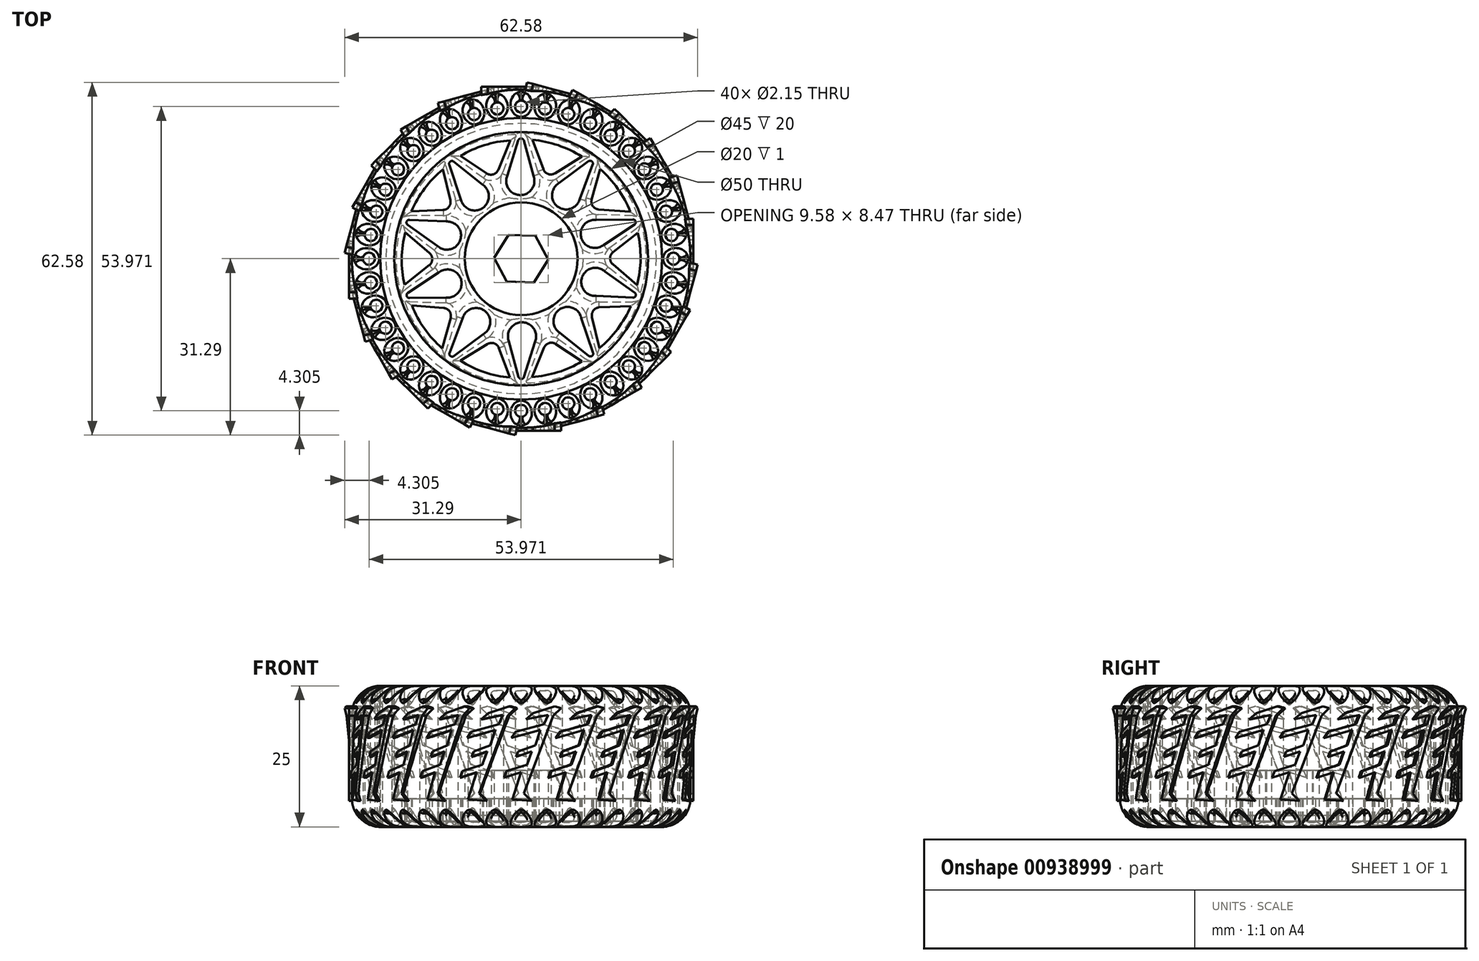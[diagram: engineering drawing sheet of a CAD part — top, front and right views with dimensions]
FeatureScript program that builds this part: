
annotation { "Feature Type Name" : "Feature", "Feature Type Description" : "" }
export const myFeature = defineFeature(function(context is Context, id is Id, definition is map)
    precondition{}
    {
        {
            var Q0;
            Q0=qCreatedBy(makeId("Top.planeOp"),FACE);
            var sketch = newSketch(context, id + "F0", { "sketchPlane" : qUnion([Q0])});
            skCircle(sketch, "E0", {"center": v(0, 0) * mm, "radius": 25 * mm});
            skCircle(sketch, "E1", {"center": v(0, 0) * mm, "radius": 22.5 * mm});
            skCircle(sketch, "E2", {"center": v(0, 0) * mm, "radius": 10 * mm});
            skLineSegment(sketch, "E3", {"start": v(0, 10) * mm, "end": v(0, 22.5) * mm, "construction": true});
            skPoint(sketch, "E4", {"position": v(0, 16.25) * mm});
            skCircle(sketch, "E5", {"center": v(-0.16, 13.78) * mm, "radius": 2.5 * mm});
            skPoint(sketch, "E6", {"position": v(0, 22.61) * mm});
            skLineSegment(sketch, "E7", {"start": v(-2.63, 14.21) * mm, "end": v(2.3, 14.21) * mm, "construction": true});
            skLineSegment(sketch, "E8", {"start": v(-0.5, 20.99) * mm, "end": v(-2.63, 14.21) * mm});
            skLineSegment(sketch, "E9", {"start": v(0.45, 20.97) * mm, "end": v(2.3, 14.21) * mm});
            skArc(sketch, "E10.filletArc", {"start": v(0.45, 20.97) * mm, "mid": v(-0.02, 21.34) * mm, "end": v(-0.5, 20.99) * mm});
            skCircle(sketch, "E11.1.0", {"center": v(-8.23, 11.06) * mm, "radius": 2.5 * mm});
            skLineSegment(sketch, "E11.1.1", {"start": v(-11.96, 17.23) * mm, "end": v(-6.49, 12.85) * mm});
            skLineSegment(sketch, "E11.1.2", {"start": v(-12.75, 16.68) * mm, "end": v(-10.48, 9.95) * mm});
            skArc(sketch, "E11.1.3", {"start": v(-11.96, 17.23) * mm, "mid": v(-12.56, 17.25) * mm, "end": v(-12.75, 16.68) * mm});
            skCircle(sketch, "E11.2.0", {"center": v(-13.15, 4.11) * mm, "radius": 2.5 * mm});
            skLineSegment(sketch, "E11.2.1", {"start": v(-19.8, 6.9) * mm, "end": v(-12.8, 6.59) * mm});
            skLineSegment(sketch, "E11.2.2", {"start": v(-20.12, 6) * mm, "end": v(-14.33, 1.9) * mm});
            skArc(sketch, "E11.2.3", {"start": v(-19.8, 6.9) * mm, "mid": v(-20.3, 6.57) * mm, "end": v(-20.12, 6) * mm});
            skCircle(sketch, "E11.3.0", {"center": v(-13.06, -4.4) * mm, "radius": 2.5 * mm});
            skLineSegment(sketch, "E11.3.1", {"start": v(-20.08, -6.05) * mm, "end": v(-14.23, -2.2) * mm});
            skLineSegment(sketch, "E11.3.2", {"start": v(-19.8, -6.97) * mm, "end": v(-12.7, -6.89) * mm});
            skArc(sketch, "E11.3.3", {"start": v(-20.08, -6.05) * mm, "mid": v(-20.29, -6.61) * mm, "end": v(-19.8, -6.97) * mm});
            skCircle(sketch, "E11.4.0", {"center": v(-7.97, -11.24) * mm, "radius": 2.5 * mm});
            skLineSegment(sketch, "E11.4.1", {"start": v(-12.7, -16.7) * mm, "end": v(-10.22, -10.14) * mm});
            skLineSegment(sketch, "E11.4.2", {"start": v(-11.92, -17.28) * mm, "end": v(-6.23, -13.04) * mm});
            skArc(sketch, "E11.4.3", {"start": v(-12.7, -16.7) * mm, "mid": v(-12.52, -17.28) * mm, "end": v(-11.92, -17.28) * mm});
            skCircle(sketch, "E11.5.0", {"center": v(0.16, -13.78) * mm, "radius": 2.5 * mm});
            skLineSegment(sketch, "E11.5.1", {"start": v(-0.45, -20.97) * mm, "end": v(-2.3, -14.21) * mm});
            skLineSegment(sketch, "E11.5.2", {"start": v(0.5, -20.99) * mm, "end": v(2.63, -14.21) * mm});
            skArc(sketch, "E11.5.3", {"start": v(-0.45, -20.97) * mm, "mid": v(0.02, -21.34) * mm, "end": v(0.5, -20.99) * mm});
            skCircle(sketch, "E11.6.0", {"center": v(8.23, -11.06) * mm, "radius": 2.5 * mm});
            skLineSegment(sketch, "E11.6.1", {"start": v(11.96, -17.23) * mm, "end": v(6.49, -12.85) * mm});
            skLineSegment(sketch, "E11.6.2", {"start": v(12.75, -16.68) * mm, "end": v(10.48, -9.95) * mm});
            skArc(sketch, "E11.6.3", {"start": v(11.96, -17.23) * mm, "mid": v(12.56, -17.25) * mm, "end": v(12.75, -16.68) * mm});
            skCircle(sketch, "E11.7.0", {"center": v(13.15, -4.11) * mm, "radius": 2.5 * mm});
            skLineSegment(sketch, "E11.7.1", {"start": v(19.8, -6.9) * mm, "end": v(12.8, -6.59) * mm});
            skLineSegment(sketch, "E11.7.2", {"start": v(20.12, -6) * mm, "end": v(14.33, -1.9) * mm});
            skArc(sketch, "E11.7.3", {"start": v(19.8, -6.9) * mm, "mid": v(20.3, -6.57) * mm, "end": v(20.12, -6) * mm});
            skCircle(sketch, "E11.8.0", {"center": v(13.06, 4.4) * mm, "radius": 2.5 * mm});
            skLineSegment(sketch, "E11.8.1", {"start": v(20.08, 6.05) * mm, "end": v(14.23, 2.2) * mm});
            skLineSegment(sketch, "E11.8.2", {"start": v(19.8, 6.97) * mm, "end": v(12.7, 6.89) * mm});
            skArc(sketch, "E11.8.3", {"start": v(20.08, 6.05) * mm, "mid": v(20.29, 6.61) * mm, "end": v(19.8, 6.97) * mm});
            skCircle(sketch, "E11.9.0", {"center": v(7.97, 11.24) * mm, "radius": 2.5 * mm});
            skLineSegment(sketch, "E11.9.1", {"start": v(12.7, 16.7) * mm, "end": v(10.22, 10.14) * mm});
            skLineSegment(sketch, "E11.9.2", {"start": v(11.92, 17.28) * mm, "end": v(6.23, 13.04) * mm});
            skArc(sketch, "E11.9.3", {"start": v(12.7, 16.7) * mm, "mid": v(12.52, 17.28) * mm, "end": v(11.92, 17.28) * mm});
            skLineSegment(sketch, "E12", {"start": v(-10.78, 18.23) * mm, "end": v(-6.12, 15.12) * mm});
            skPoint(sketch, "E12.endSnap0", {"position": v(-9.22, 15.04) * mm});
            skLineSegment(sketch, "E13", {"start": v(-1.93, 20.97) * mm, "end": v(-4.06, 15.78) * mm});
            skArc(sketch, "E14", {"start": v(-6.12, 15.12) * mm, "mid": v(-4.94, 14.97) * mm, "end": v(-4.06, 15.78) * mm});
            skArc(sketch, "E15", {"start": v(-1.93, 20.97) * mm, "mid": v(-6.52, 20.14) * mm, "end": v(-10.78, 18.23) * mm});
            skLineSegment(sketch, "E16.1.0", {"start": v(-19.44, 8.41) * mm, "end": v(-13.84, 8.64) * mm});
            skArc(sketch, "E16.1.1", {"start": v(-13.84, 8.64) * mm, "mid": v(-12.8, 9.21) * mm, "end": v(-12.56, 10.38) * mm});
            skLineSegment(sketch, "E16.1.2", {"start": v(-13.9, 15.83) * mm, "end": v(-12.56, 10.38) * mm});
            skArc(sketch, "E16.1.3", {"start": v(-13.9, 15.83) * mm, "mid": v(-17.11, 12.46) * mm, "end": v(-19.44, 8.41) * mm});
            skLineSegment(sketch, "E16.2.0", {"start": v(-20.67, -4.62) * mm, "end": v(-16.27, -1.15) * mm});
            skArc(sketch, "E16.2.1", {"start": v(-16.27, -1.15) * mm, "mid": v(-15.76, -0.07) * mm, "end": v(-16.26, 1.01) * mm});
            skLineSegment(sketch, "E16.2.2", {"start": v(-20.54, 4.65) * mm, "end": v(-16.26, 1.01) * mm});
            skArc(sketch, "E16.2.3", {"start": v(-20.54, 4.65) * mm, "mid": v(-21.17, 0.02) * mm, "end": v(-20.67, -4.62) * mm});
            skLineSegment(sketch, "E16.3.0", {"start": v(-14, -15.89) * mm, "end": v(-12.5, -10.5) * mm});
            skArc(sketch, "E16.3.1", {"start": v(-12.5, -10.5) * mm, "mid": v(-12.71, -9.32) * mm, "end": v(-13.75, -8.74) * mm});
            skLineSegment(sketch, "E16.3.2", {"start": v(-19.35, -8.32) * mm, "end": v(-13.75, -8.74) * mm});
            skArc(sketch, "E16.3.3", {"start": v(-19.35, -8.32) * mm, "mid": v(-17.14, -12.42) * mm, "end": v(-14, -15.89) * mm});
            skLineSegment(sketch, "E16.4.0", {"start": v(-2, -21.09) * mm, "end": v(-3.94, -15.83) * mm});
            skArc(sketch, "E16.4.1", {"start": v(-3.94, -15.83) * mm, "mid": v(-4.8, -15.01) * mm, "end": v(-5.99, -15.15) * mm});
            skLineSegment(sketch, "E16.4.2", {"start": v(-10.77, -18.1) * mm, "end": v(-5.99, -15.15) * mm});
            skArc(sketch, "E16.4.3", {"start": v(-10.77, -18.1) * mm, "mid": v(-6.56, -20.12) * mm, "end": v(-2, -21.09) * mm});
            skLineSegment(sketch, "E16.5.0", {"start": v(10.78, -18.23) * mm, "end": v(6.12, -15.12) * mm});
            skArc(sketch, "E16.5.1", {"start": v(6.12, -15.12) * mm, "mid": v(4.94, -14.97) * mm, "end": v(4.06, -15.78) * mm});
            skLineSegment(sketch, "E16.5.2", {"start": v(1.93, -20.97) * mm, "end": v(4.06, -15.78) * mm});
            skArc(sketch, "E16.5.3", {"start": v(1.93, -20.97) * mm, "mid": v(6.52, -20.14) * mm, "end": v(10.78, -18.23) * mm});
            skLineSegment(sketch, "E16.6.0", {"start": v(19.44, -8.41) * mm, "end": v(13.84, -8.64) * mm});
            skArc(sketch, "E16.6.1", {"start": v(13.84, -8.64) * mm, "mid": v(12.8, -9.21) * mm, "end": v(12.56, -10.38) * mm});
            skLineSegment(sketch, "E16.6.2", {"start": v(13.9, -15.83) * mm, "end": v(12.56, -10.38) * mm});
            skArc(sketch, "E16.6.3", {"start": v(13.9, -15.83) * mm, "mid": v(17.11, -12.46) * mm, "end": v(19.44, -8.41) * mm});
            skLineSegment(sketch, "E16.7.0", {"start": v(20.67, 4.62) * mm, "end": v(16.27, 1.15) * mm});
            skArc(sketch, "E16.7.1", {"start": v(16.27, 1.15) * mm, "mid": v(15.76, 0.07) * mm, "end": v(16.26, -1.01) * mm});
            skLineSegment(sketch, "E16.7.2", {"start": v(20.54, -4.65) * mm, "end": v(16.26, -1.01) * mm});
            skArc(sketch, "E16.7.3", {"start": v(20.54, -4.65) * mm, "mid": v(21.17, -0.02) * mm, "end": v(20.67, 4.62) * mm});
            skLineSegment(sketch, "E16.8.0", {"start": v(14, 15.89) * mm, "end": v(12.5, 10.5) * mm});
            skArc(sketch, "E16.8.1", {"start": v(12.5, 10.5) * mm, "mid": v(12.71, 9.32) * mm, "end": v(13.75, 8.74) * mm});
            skLineSegment(sketch, "E16.8.2", {"start": v(19.35, 8.32) * mm, "end": v(13.75, 8.74) * mm});
            skArc(sketch, "E16.8.3", {"start": v(19.35, 8.32) * mm, "mid": v(17.14, 12.42) * mm, "end": v(14, 15.89) * mm});
            skLineSegment(sketch, "E16.9.0", {"start": v(2, 21.09) * mm, "end": v(3.94, 15.83) * mm});
            skArc(sketch, "E16.9.1", {"start": v(3.94, 15.83) * mm, "mid": v(4.8, 15.01) * mm, "end": v(5.99, 15.15) * mm});
            skLineSegment(sketch, "E16.9.2", {"start": v(10.77, 18.1) * mm, "end": v(5.99, 15.15) * mm});
            skArc(sketch, "E16.9.3", {"start": v(10.77, 18.1) * mm, "mid": v(6.56, 20.12) * mm, "end": v(2, 21.09) * mm});
            skCircle(sketch, "E17", {"center": v(0, 0) * mm, "radius": 30 * mm});
            skSolve(sketch);
        }
        {
            var Q0;
            Q0=makeQuery(id+"F0.imprint","IMPRINT",FACE,{"disambiguationData":[TD([[makeQuery(id+"F0.imprint","IMPRINT",EDGE,{"derivedFrom":sQuery(id+"F0.wireOp",EDGE,"E0")}),1.0]])]});
            extrude(context, id + "F1", {"entities" : qUnion([Q0]), "depth" : 25 * mm, "offsetDistance" : 25 * mm});
        }
        {
            var Q0;
            Q0=makeQuery(id+"F0.imprint","IMPRINT",FACE,{"disambiguationData":[TD([[makeQuery(id+"F0.imprint","IMPRINT",EDGE,{"derivedFrom":sQuery(id+"F0.wireOp",EDGE,"E1")}),1.0]])]});
            extrude(context, id + "F2", {"entities" : qUnion([Q0]), "operationType" : NewBodyOperationType.ADD, "depth" : 5 * mm, "offsetDistance" : 25 * mm});
        }
        {
            var Q0;
            {var subQ0=sQuery(id+"F0.wireOp",EDGE,"E2");var subQ1=makeQuery(id+"F0.imprint","INTERSECT",VERTEX,{"derivedFrom":[subQ0,sQuery(id+"F0.wireOp",EDGE,"FMw9U3Ag-M4uU-eOUw-AIyu-Y3kzjyrUIhWa.right")]});Q0=makeQuery(id+"F0.imprint","IMPRINT",FACE,{"disambiguationData":[TD([[makeQuery(id+"F0.imprint","IMPRINT",EDGE,{"disambiguationData":[TD([[subQ1,1.0]])],"derivedFrom":subQ0}),1.0]])]});}
            extrude(context, id + "F3", {"entities" : qUnion([Q0]), "operationType" : NewBodyOperationType.ADD, "depth" : 10 * mm, "offsetDistance" : 25 * mm});
        }
        {
            var Q0;
            Q0=makeQuery(id+"F0.imprint","IMPRINT",FACE,{"disambiguationData":[TD([[makeQuery(id+"F0.imprint","IMPRINT",EDGE,{"derivedFrom":sQuery(id+"F0.wireOp",EDGE,"E2")}),1.0]])]});
            extrude(context, id + "F4", {"entities" : qUnion([Q0]), "operationType" : NewBodyOperationType.REMOVE, "depth" : 2 * mm, "offsetDistance" : 25 * mm});
        }
        {
            var Q0;
            Q0=makeQuery(id+"F0.imprint","IMPRINT",FACE,{"disambiguationData":[TD([[makeQuery(id+"F0.imprint","IMPRINT",EDGE,{"derivedFrom":sQuery(id+"F0.wireOp",EDGE,"E2")}),1.0]])]});
            var sketch = newSketch(context, id + "F5", { "sketchPlane" : qUnion([Q0])});
            skPoint(sketch, "E18.0.midPoint", {"position": v(-3.35, 1.99) * mm});
            skCircle(sketch, "E19.cCircle", {"center": v(0, 0) * mm, "radius": 4.15 * mm, "construction": true});
            skLineSegment(sketch, "E19.0", {"start": v(-4.79, 0.17) * mm, "end": v(-2.25, 4.23) * mm});
            skLineSegment(sketch, "E19.1", {"start": v(-2.25, 4.23) * mm, "end": v(2.54, 4.06) * mm});
            skLineSegment(sketch, "E19.2", {"start": v(2.54, 4.06) * mm, "end": v(4.79, -0.17) * mm});
            skLineSegment(sketch, "E19.3", {"start": v(4.79, -0.17) * mm, "end": v(2.25, -4.23) * mm});
            skLineSegment(sketch, "E19.4", {"start": v(2.25, -4.23) * mm, "end": v(-2.54, -4.06) * mm});
            skLineSegment(sketch, "E19.5", {"start": v(-2.54, -4.06) * mm, "end": v(-4.79, 0.17) * mm});
            skPoint(sketch, "E19.0.midPoint", {"position": v(-3.52, 2.2) * mm});
            skPoint(sketch, "E20.orphan", {"position": v(-2.3, -3.87) * mm});
            skPoint(sketch, "E21.orphan", {"position": v(2.2, -3.92) * mm});
            skPoint(sketch, "E22.orphan", {"position": v(-4.5, 0.05) * mm});
            skPoint(sketch, "E18.1.start.orphan", {"position": v(-2.2, 3.92) * mm});
            skSolve(sketch);
        }
        {
            var Q0;
            Q0=makeQuery(id+"F5.imprint","IMPRINT",FACE,{"disambiguationData":[TD([[makeQuery(id+"F5.imprint","IMPRINT",EDGE,{"derivedFrom":sQuery(id+"F5.wireOp",EDGE,"E19.0")}),-1.0]])]});
            extrude(context, id + "F6", {"entities" : qUnion([Q0]), "operationType" : NewBodyOperationType.REMOVE, "depth" : 25 * mm, "offsetDistance" : 25 * mm});
        }
        {
            var Q0;
            {var subQ0=sQuery(id+"F0.wireOp",EDGE,"E2");var subQ1=sQuery(id+"F0.wireOp",EDGE,"E1");Q0=makeQuery(id+"F3.boolean.opBoolean","MERGE",FACE,{"derivedFrom":[makeQuery(id+"F2.boolean.opBoolean","MERGE",FACE,{"derivedFrom":[makeQuery(id+"F1.opExtrude","CAP_FACE",FACE,{"disambiguationData":[OSD([sQuery(id+"F0.wireOp",EDGE,"E0"),subQ1])],"isStart":true}),makeQuery(id+"F2.opExtrude","CAP_FACE",FACE,{"disambiguationData":[OSD([subQ1,subQ0,sQuery(id+"F0.wireOp",EDGE,"E5"),sQuery(id+"F0.wireOp",EDGE,"E8"),sQuery(id+"F0.wireOp",EDGE,"E9"),sQuery(id+"F0.wireOp",EDGE,"E10.filletArc"),sQuery(id+"F0.wireOp",EDGE,"E11.1.0"),sQuery(id+"F0.wireOp",EDGE,"E11.1.1"),sQuery(id+"F0.wireOp",EDGE,"E11.1.2"),sQuery(id+"F0.wireOp",EDGE,"E11.1.3"),sQuery(id+"F0.wireOp",EDGE,"E11.2.0"),sQuery(id+"F0.wireOp",EDGE,"E11.2.1"),sQuery(id+"F0.wireOp",EDGE,"E11.2.2"),sQuery(id+"F0.wireOp",EDGE,"E11.2.3"),sQuery(id+"F0.wireOp",EDGE,"E11.3.0"),sQuery(id+"F0.wireOp",EDGE,"E11.3.1"),sQuery(id+"F0.wireOp",EDGE,"E11.3.2"),sQuery(id+"F0.wireOp",EDGE,"E11.3.3"),sQuery(id+"F0.wireOp",EDGE,"E11.4.0"),sQuery(id+"F0.wireOp",EDGE,"E11.4.1"),sQuery(id+"F0.wireOp",EDGE,"E11.4.2"),sQuery(id+"F0.wireOp",EDGE,"E11.4.3"),sQuery(id+"F0.wireOp",EDGE,"E11.5.0"),sQuery(id+"F0.wireOp",EDGE,"E11.5.1"),sQuery(id+"F0.wireOp",EDGE,"E11.5.2"),sQuery(id+"F0.wireOp",EDGE,"E11.5.3"),sQuery(id+"F0.wireOp",EDGE,"E11.6.0"),sQuery(id+"F0.wireOp",EDGE,"E11.6.1"),sQuery(id+"F0.wireOp",EDGE,"E11.6.2"),sQuery(id+"F0.wireOp",EDGE,"E11.6.3"),sQuery(id+"F0.wireOp",EDGE,"E11.7.0"),sQuery(id+"F0.wireOp",EDGE,"E11.7.1"),sQuery(id+"F0.wireOp",EDGE,"E11.7.2"),sQuery(id+"F0.wireOp",EDGE,"E11.7.3"),sQuery(id+"F0.wireOp",EDGE,"E11.8.0"),sQuery(id+"F0.wireOp",EDGE,"E11.8.1"),sQuery(id+"F0.wireOp",EDGE,"E11.8.2"),sQuery(id+"F0.wireOp",EDGE,"E11.8.3"),sQuery(id+"F0.wireOp",EDGE,"E11.9.0"),sQuery(id+"F0.wireOp",EDGE,"E11.9.1"),sQuery(id+"F0.wireOp",EDGE,"E11.9.2"),sQuery(id+"F0.wireOp",EDGE,"E11.9.3"),sQuery(id+"F0.wireOp",EDGE,"E12"),sQuery(id+"F0.wireOp",EDGE,"E13"),sQuery(id+"F0.wireOp",EDGE,"E14"),sQuery(id+"F0.wireOp",EDGE,"E15"),sQuery(id+"F0.wireOp",EDGE,"E16.1.0"),sQuery(id+"F0.wireOp",EDGE,"E16.1.1"),sQuery(id+"F0.wireOp",EDGE,"E16.1.2"),sQuery(id+"F0.wireOp",EDGE,"E16.1.3"),sQuery(id+"F0.wireOp",EDGE,"E16.2.0"),sQuery(id+"F0.wireOp",EDGE,"E16.2.1"),sQuery(id+"F0.wireOp",EDGE,"E16.2.2"),sQuery(id+"F0.wireOp",EDGE,"E16.2.3"),sQuery(id+"F0.wireOp",EDGE,"E16.3.0"),sQuery(id+"F0.wireOp",EDGE,"E16.3.1"),sQuery(id+"F0.wireOp",EDGE,"E16.3.2"),sQuery(id+"F0.wireOp",EDGE,"E16.3.3"),sQuery(id+"F0.wireOp",EDGE,"E16.4.0"),sQuery(id+"F0.wireOp",EDGE,"E16.4.1"),sQuery(id+"F0.wireOp",EDGE,"E16.4.2"),sQuery(id+"F0.wireOp",EDGE,"E16.4.3"),sQuery(id+"F0.wireOp",EDGE,"E16.5.0"),sQuery(id+"F0.wireOp",EDGE,"E16.5.1"),sQuery(id+"F0.wireOp",EDGE,"E16.5.2"),sQuery(id+"F0.wireOp",EDGE,"E16.5.3"),sQuery(id+"F0.wireOp",EDGE,"E16.6.0"),sQuery(id+"F0.wireOp",EDGE,"E16.6.1"),sQuery(id+"F0.wireOp",EDGE,"E16.6.2"),sQuery(id+"F0.wireOp",EDGE,"E16.6.3"),sQuery(id+"F0.wireOp",EDGE,"E16.7.0"),sQuery(id+"F0.wireOp",EDGE,"E16.7.1"),sQuery(id+"F0.wireOp",EDGE,"E16.7.2"),sQuery(id+"F0.wireOp",EDGE,"E16.7.3"),sQuery(id+"F0.wireOp",EDGE,"E16.8.0"),sQuery(id+"F0.wireOp",EDGE,"E16.8.1"),sQuery(id+"F0.wireOp",EDGE,"E16.8.2"),sQuery(id+"F0.wireOp",EDGE,"E16.8.3"),sQuery(id+"F0.wireOp",EDGE,"E16.9.0"),sQuery(id+"F0.wireOp",EDGE,"E16.9.1"),sQuery(id+"F0.wireOp",EDGE,"E16.9.2"),sQuery(id+"F0.wireOp",EDGE,"E16.9.3")])],"isStart":true})]}),makeQuery(id+"F3.opExtrude","CAP_FACE",FACE,{"disambiguationData":[OSD([subQ0])],"isStart":true})]});}
            chamfer(context, id + "F7", {"entities" : qUnion([Q0]), "width" : 1 * mm, "tangentPropagation" : true});
        }
        {
            var Q0;
            Q0=makeQuery(id+"F0.imprint","IMPRINT",FACE,{"disambiguationData":[TD([[makeQuery(id+"F0.imprint","IMPRINT",EDGE,{"derivedFrom":sQuery(id+"F0.wireOp",EDGE,"E0")}),-1.0]])]});
            extrude(context, id + "F8", {"entities" : qUnion([Q0]), "depth" : 25 * mm, "offsetDistance" : 25 * mm});
        }
        {
            var Q0;
            Q0=makeQuery(id+"F8.opExtrude","CAP_EDGE",EDGE,{"disambiguationData":[OSD([sQuery(id+"F0.wireOp",EDGE,"E17")])],"isStart":true});
            var Q1;
            Q1=makeQuery(id+"F8.opExtrude","CAP_EDGE",EDGE,{"disambiguationData":[OSD([sQuery(id+"F0.wireOp",EDGE,"E17")])],"isStart":false});
            fillet(context, id + "F9", {"entities" : qUnion([Q0, Q1]), "radius" : 5 * mm, "tangentPropagation" : true, "defaultsChanged" : false, "vertexSettings" : [], "allowEdgeOverflow" : false});
        }
        {
            var Q0;
            Q0=qCreatedBy(makeId("Right.planeOp"),FACE);
            cPlane(context, id + "F10", {"entities" : qUnion([Q0]), "cplaneType" : CPlaneType.OFFSET, "offset" : 30.5 * mm, "width" : 150 * mm, "height" : 150 * mm});
        }
        {
            var Q0;
            Q0=qCreatedBy(id+"F10.planeOp",FACE);
            var sketch = newSketch(context, id + "F11", { "sketchPlane" : qUnion([Q0])});
            skLineSegment(sketch, "E23", {"start": v(-1.56, 4.84) * mm, "end": v(0, 9.7) * mm});
            skLineSegment(sketch, "E24", {"start": v(0, 9.7) * mm, "end": v(-3.04, 8.74) * mm});
            skLineSegment(sketch, "E25", {"start": v(-3.04, 8.74) * mm, "end": v(-2.61, 9.85) * mm});
            skLineSegment(sketch, "E26", {"start": v(-2.61, 9.85) * mm, "end": v(1.04, 11.05) * mm});
            skLineSegment(sketch, "E27", {"start": v(1.04, 11.05) * mm, "end": v(1.9, 13.36) * mm});
            skLineSegment(sketch, "E28", {"start": v(1.9, 13.36) * mm, "end": v(-0.94, 12.43) * mm});
            skLineSegment(sketch, "E29", {"start": v(-0.94, 12.43) * mm, "end": v(-0.56, 13.36) * mm});
            skLineSegment(sketch, "E30", {"start": v(-0.56, 13.36) * mm, "end": v(2.5, 14.44) * mm});
            skLineSegment(sketch, "E31", {"start": v(2.5, 14.44) * mm, "end": v(3.39, 17.2) * mm});
            skLineSegment(sketch, "E32", {"start": v(3.39, 17.2) * mm, "end": v(-1.72, 15.78) * mm});
            skLineSegment(sketch, "E33", {"start": v(-1.72, 15.78) * mm, "end": v(-0.97, 16.86) * mm});
            skLineSegment(sketch, "E34", {"start": v(-0.97, 16.86) * mm, "end": v(4.06, 18.2) * mm});
            skLineSegment(sketch, "E35", {"start": v(4.06, 18.2) * mm, "end": v(4.77, 19.88) * mm});
            skLineSegment(sketch, "E36", {"start": v(4.77, 19.88) * mm, "end": v(0.85, 19.06) * mm});
            skLineSegment(sketch, "E37", {"start": v(0.85, 19.06) * mm, "end": v(2.16, 20.18) * mm});
            skLineSegment(sketch, "E38", {"start": v(2.16, 20.18) * mm, "end": v(5.96, 21.37) * mm});
            skLineSegment(sketch, "E39", {"start": v(5.96, 21.37) * mm, "end": v(7.08, 21.04) * mm});
            skLineSegment(sketch, "E40", {"start": v(7.08, 21.04) * mm, "end": v(5.7, 19.73) * mm});
            skLineSegment(sketch, "E41", {"start": v(5.7, 19.73) * mm, "end": v(0.48, 5.94) * mm});
            skLineSegment(sketch, "E42", {"start": v(0.48, 5.94) * mm, "end": v(1.79, 4.63) * mm});
            skLineSegment(sketch, "E43", {"start": v(1.79, 4.63) * mm, "end": v(-1.56, 4.84) * mm});
            skSolve(sketch);
        }
        {
            var Q0;
            Q0=qCreatedBy(makeId("Right.planeOp"),FACE);
            var sketch = newSketch(context, id + "F12", { "sketchPlane" : qUnion([Q0])});
            skLineSegment(sketch, "E44", {"start": v(0, 0) * mm, "end": v(0, 40.56) * mm});
            skSolve(sketch);
        }
        {
            var Q0;
            Q0=makeQuery(id+"F11.imprint","IMPRINT",FACE,{"disambiguationData":[TD([[makeQuery(id+"F11.imprint","IMPRINT",EDGE,{"derivedFrom":sQuery(id+"F11.wireOp",EDGE,"E23")}),-1.0]])]});
            extrude(context, id + "F13", {"entities" : qUnion([Q0]), "oppositeDirection" : true, "depth" : 2 * mm, "offsetDistance" : 25 * mm});
        }
        {
            var Q0;
            Q0=makeQuery(id+"F13.opExtrude","SWEPT_BODY",BODY,{"disambiguationData":[OSD([sQuery(id+"F11.wireOp",EDGE,"E23"),sQuery(id+"F11.wireOp",EDGE,"E24"),sQuery(id+"F11.wireOp",EDGE,"E25"),sQuery(id+"F11.wireOp",EDGE,"E26"),sQuery(id+"F11.wireOp",EDGE,"E27"),sQuery(id+"F11.wireOp",EDGE,"E28"),sQuery(id+"F11.wireOp",EDGE,"E29"),sQuery(id+"F11.wireOp",EDGE,"E30"),sQuery(id+"F11.wireOp",EDGE,"E31"),sQuery(id+"F11.wireOp",EDGE,"E32"),sQuery(id+"F11.wireOp",EDGE,"E33"),sQuery(id+"F11.wireOp",EDGE,"E34"),sQuery(id+"F11.wireOp",EDGE,"E35"),sQuery(id+"F11.wireOp",EDGE,"E36"),sQuery(id+"F11.wireOp",EDGE,"E37"),sQuery(id+"F11.wireOp",EDGE,"E38"),sQuery(id+"F11.wireOp",EDGE,"E39"),sQuery(id+"F11.wireOp",EDGE,"E40"),sQuery(id+"F11.wireOp",EDGE,"E41"),sQuery(id+"F11.wireOp",EDGE,"E42"),sQuery(id+"F11.wireOp",EDGE,"E43")])]});
            var Q1;
            Q1=sQuery(id+"F12.wireOp",EDGE,"E44");
            circularPattern(context, id + "F14", {"operationType" : NewBodyOperationType.ADD, "entities" : qUnion([Q0]), "axis" : qUnion([Q1]), "angle" : 360 * degree, "instanceCount" : 24, "equalSpace" : true});
        }
        {
            var Q0;
            Q0=qCreatedBy(makeId("Top.planeOp"),FACE);
            var sketch = newSketch(context, id + "F15", { "sketchPlane" : qUnion([Q0])});
            skCircle(sketch, "E45", {"center": v(0, 0) * mm, "radius": 26.99 * mm, "construction": true});
            skCircle(sketch, "E46", {"center": v(0, -26.99) * mm, "radius": 1.07 * mm});
            skCircle(sketch, "E47.1.0", {"center": v(4.22, -26.65) * mm, "radius": 1.07 * mm});
            skCircle(sketch, "E47.2.0", {"center": v(8.34, -25.66) * mm, "radius": 1.07 * mm});
            skCircle(sketch, "E47.3.0", {"center": v(12.25, -24.04) * mm, "radius": 1.07 * mm});
            skCircle(sketch, "E47.4.0", {"center": v(15.86, -21.83) * mm, "radius": 1.07 * mm});
            skCircle(sketch, "E47.5.0", {"center": v(19.08, -19.08) * mm, "radius": 1.07 * mm});
            skCircle(sketch, "E47.6.0", {"center": v(21.83, -15.86) * mm, "radius": 1.07 * mm});
            skCircle(sketch, "E47.7.0", {"center": v(24.04, -12.25) * mm, "radius": 1.07 * mm});
            skCircle(sketch, "E47.8.0", {"center": v(25.66, -8.34) * mm, "radius": 1.07 * mm});
            skCircle(sketch, "E47.9.0", {"center": v(26.65, -4.22) * mm, "radius": 1.07 * mm});
            skCircle(sketch, "E47.10.0", {"center": v(26.99, 0) * mm, "radius": 1.07 * mm});
            skCircle(sketch, "E47.11.0", {"center": v(26.65, 4.22) * mm, "radius": 1.07 * mm});
            skCircle(sketch, "E47.12.0", {"center": v(25.66, 8.34) * mm, "radius": 1.07 * mm});
            skCircle(sketch, "E47.13.0", {"center": v(24.04, 12.25) * mm, "radius": 1.07 * mm});
            skCircle(sketch, "E47.14.0", {"center": v(21.83, 15.86) * mm, "radius": 1.07 * mm});
            skCircle(sketch, "E47.15.0", {"center": v(19.08, 19.08) * mm, "radius": 1.07 * mm});
            skCircle(sketch, "E47.16.0", {"center": v(15.86, 21.83) * mm, "radius": 1.07 * mm});
            skCircle(sketch, "E47.17.0", {"center": v(12.25, 24.04) * mm, "radius": 1.07 * mm});
            skCircle(sketch, "E47.18.0", {"center": v(8.34, 25.66) * mm, "radius": 1.07 * mm});
            skCircle(sketch, "E47.19.0", {"center": v(4.22, 26.65) * mm, "radius": 1.07 * mm});
            skCircle(sketch, "E48.1.20.0", {"center": v(0, 26.99) * mm, "radius": 1.07 * mm});
            skCircle(sketch, "E48.1.21.0", {"center": v(-4.22, 26.65) * mm, "radius": 1.07 * mm});
            skCircle(sketch, "E48.1.22.0", {"center": v(-8.34, 25.66) * mm, "radius": 1.07 * mm});
            skCircle(sketch, "E48.1.23.0", {"center": v(-12.25, 24.04) * mm, "radius": 1.07 * mm});
            skCircle(sketch, "E48.1.24.0", {"center": v(-15.86, 21.83) * mm, "radius": 1.07 * mm});
            skCircle(sketch, "E48.1.25.0", {"center": v(-19.08, 19.08) * mm, "radius": 1.07 * mm});
            skCircle(sketch, "E48.1.26.0", {"center": v(-21.83, 15.86) * mm, "radius": 1.07 * mm});
            skCircle(sketch, "E48.1.27.0", {"center": v(-24.04, 12.25) * mm, "radius": 1.07 * mm});
            skCircle(sketch, "E48.1.28.0", {"center": v(-25.66, 8.34) * mm, "radius": 1.07 * mm});
            skCircle(sketch, "E48.1.29.0", {"center": v(-26.65, 4.22) * mm, "radius": 1.07 * mm});
            skCircle(sketch, "E49.1.30.0", {"center": v(-26.99, 0) * mm, "radius": 1.07 * mm});
            skCircle(sketch, "E49.1.31.0", {"center": v(-26.65, -4.22) * mm, "radius": 1.07 * mm});
            skCircle(sketch, "E49.1.32.0", {"center": v(-25.66, -8.34) * mm, "radius": 1.07 * mm});
            skCircle(sketch, "E49.1.33.0", {"center": v(-24.04, -12.25) * mm, "radius": 1.07 * mm});
            skCircle(sketch, "E49.1.34.0", {"center": v(-21.83, -15.86) * mm, "radius": 1.07 * mm});
            skCircle(sketch, "E49.1.35.0", {"center": v(-19.08, -19.08) * mm, "radius": 1.07 * mm});
            skCircle(sketch, "E49.1.36.0", {"center": v(-15.86, -21.83) * mm, "radius": 1.07 * mm});
            skCircle(sketch, "E49.1.37.0", {"center": v(-12.25, -24.04) * mm, "radius": 1.07 * mm});
            skCircle(sketch, "E49.1.38.0", {"center": v(-8.34, -25.66) * mm, "radius": 1.07 * mm});
            skCircle(sketch, "E49.1.39.0", {"center": v(-4.22, -26.65) * mm, "radius": 1.07 * mm});
            skSolve(sketch);
        }
        {
            var Q0;
            Q0=makeQuery(id+"F15.imprint","IMPRINT",FACE,{"disambiguationData":[TD([[makeQuery(id+"F15.imprint","IMPRINT",EDGE,{"derivedFrom":sQuery(id+"F15.wireOp",EDGE,"E49.1.39.0")}),1.0]])]});
            var Q1;
            Q1=makeQuery(id+"F15.imprint","IMPRINT",FACE,{"disambiguationData":[TD([[makeQuery(id+"F15.imprint","IMPRINT",EDGE,{"derivedFrom":sQuery(id+"F15.wireOp",EDGE,"E46")}),1.0]])]});
            var Q2;
            Q2=makeQuery(id+"F15.imprint","IMPRINT",FACE,{"disambiguationData":[TD([[makeQuery(id+"F15.imprint","IMPRINT",EDGE,{"derivedFrom":sQuery(id+"F15.wireOp",EDGE,"E47.1.0")}),1.0]])]});
            var Q3;
            Q3=makeQuery(id+"F15.imprint","IMPRINT",FACE,{"disambiguationData":[TD([[makeQuery(id+"F15.imprint","IMPRINT",EDGE,{"derivedFrom":sQuery(id+"F15.wireOp",EDGE,"E47.2.0")}),1.0]])]});
            var Q4;
            Q4=makeQuery(id+"F15.imprint","IMPRINT",FACE,{"disambiguationData":[TD([[makeQuery(id+"F15.imprint","IMPRINT",EDGE,{"derivedFrom":sQuery(id+"F15.wireOp",EDGE,"E47.3.0")}),1.0]])]});
            var Q5;
            Q5=makeQuery(id+"F15.imprint","IMPRINT",FACE,{"disambiguationData":[TD([[makeQuery(id+"F15.imprint","IMPRINT",EDGE,{"derivedFrom":sQuery(id+"F15.wireOp",EDGE,"E47.4.0")}),1.0]])]});
            var Q6;
            Q6=makeQuery(id+"F15.imprint","IMPRINT",FACE,{"disambiguationData":[TD([[makeQuery(id+"F15.imprint","IMPRINT",EDGE,{"derivedFrom":sQuery(id+"F15.wireOp",EDGE,"E47.5.0")}),1.0]])]});
            var Q7;
            Q7=makeQuery(id+"F15.imprint","IMPRINT",FACE,{"disambiguationData":[TD([[makeQuery(id+"F15.imprint","IMPRINT",EDGE,{"derivedFrom":sQuery(id+"F15.wireOp",EDGE,"E47.6.0")}),1.0]])]});
            var Q8;
            Q8=makeQuery(id+"F15.imprint","IMPRINT",FACE,{"disambiguationData":[TD([[makeQuery(id+"F15.imprint","IMPRINT",EDGE,{"derivedFrom":sQuery(id+"F15.wireOp",EDGE,"E47.7.0")}),1.0]])]});
            var Q9;
            Q9=makeQuery(id+"F15.imprint","IMPRINT",FACE,{"disambiguationData":[TD([[makeQuery(id+"F15.imprint","IMPRINT",EDGE,{"derivedFrom":sQuery(id+"F15.wireOp",EDGE,"E47.8.0")}),1.0]])]});
            var Q10;
            Q10=makeQuery(id+"F15.imprint","IMPRINT",FACE,{"disambiguationData":[TD([[makeQuery(id+"F15.imprint","IMPRINT",EDGE,{"derivedFrom":sQuery(id+"F15.wireOp",EDGE,"E47.9.0")}),1.0]])]});
            var Q11;
            Q11=makeQuery(id+"F15.imprint","IMPRINT",FACE,{"disambiguationData":[TD([[makeQuery(id+"F15.imprint","IMPRINT",EDGE,{"derivedFrom":sQuery(id+"F15.wireOp",EDGE,"E47.10.0")}),1.0]])]});
            var Q12;
            Q12=makeQuery(id+"F15.imprint","IMPRINT",FACE,{"disambiguationData":[TD([[makeQuery(id+"F15.imprint","IMPRINT",EDGE,{"derivedFrom":sQuery(id+"F15.wireOp",EDGE,"E47.11.0")}),1.0]])]});
            var Q13;
            Q13=makeQuery(id+"F15.imprint","IMPRINT",FACE,{"disambiguationData":[TD([[makeQuery(id+"F15.imprint","IMPRINT",EDGE,{"derivedFrom":sQuery(id+"F15.wireOp",EDGE,"E47.12.0")}),1.0]])]});
            var Q14;
            Q14=makeQuery(id+"F15.imprint","IMPRINT",FACE,{"disambiguationData":[TD([[makeQuery(id+"F15.imprint","IMPRINT",EDGE,{"derivedFrom":sQuery(id+"F15.wireOp",EDGE,"E47.13.0")}),1.0]])]});
            var Q15;
            Q15=makeQuery(id+"F15.imprint","IMPRINT",FACE,{"disambiguationData":[TD([[makeQuery(id+"F15.imprint","IMPRINT",EDGE,{"derivedFrom":sQuery(id+"F15.wireOp",EDGE,"E47.14.0")}),1.0]])]});
            var Q16;
            Q16=makeQuery(id+"F15.imprint","IMPRINT",FACE,{"disambiguationData":[TD([[makeQuery(id+"F15.imprint","IMPRINT",EDGE,{"derivedFrom":sQuery(id+"F15.wireOp",EDGE,"E47.15.0")}),1.0]])]});
            var Q17;
            Q17=makeQuery(id+"F15.imprint","IMPRINT",FACE,{"disambiguationData":[TD([[makeQuery(id+"F15.imprint","IMPRINT",EDGE,{"derivedFrom":sQuery(id+"F15.wireOp",EDGE,"E47.16.0")}),1.0]])]});
            var Q18;
            Q18=makeQuery(id+"F15.imprint","IMPRINT",FACE,{"disambiguationData":[TD([[makeQuery(id+"F15.imprint","IMPRINT",EDGE,{"derivedFrom":sQuery(id+"F15.wireOp",EDGE,"E47.17.0")}),1.0]])]});
            var Q19;
            Q19=makeQuery(id+"F15.imprint","IMPRINT",FACE,{"disambiguationData":[TD([[makeQuery(id+"F15.imprint","IMPRINT",EDGE,{"derivedFrom":sQuery(id+"F15.wireOp",EDGE,"E47.18.0")}),1.0]])]});
            var Q20;
            Q20=makeQuery(id+"F15.imprint","IMPRINT",FACE,{"disambiguationData":[TD([[makeQuery(id+"F15.imprint","IMPRINT",EDGE,{"derivedFrom":sQuery(id+"F15.wireOp",EDGE,"E47.19.0")}),1.0]])]});
            var Q21;
            Q21=makeQuery(id+"F15.imprint","IMPRINT",FACE,{"disambiguationData":[TD([[makeQuery(id+"F15.imprint","IMPRINT",EDGE,{"derivedFrom":sQuery(id+"F15.wireOp",EDGE,"E48.1.20.0")}),1.0]])]});
            var Q22;
            Q22=makeQuery(id+"F15.imprint","IMPRINT",FACE,{"disambiguationData":[TD([[makeQuery(id+"F15.imprint","IMPRINT",EDGE,{"derivedFrom":sQuery(id+"F15.wireOp",EDGE,"E48.1.21.0")}),1.0]])]});
            var Q23;
            Q23=makeQuery(id+"F15.imprint","IMPRINT",FACE,{"disambiguationData":[TD([[makeQuery(id+"F15.imprint","IMPRINT",EDGE,{"derivedFrom":sQuery(id+"F15.wireOp",EDGE,"E48.1.24.0")}),1.0]])]});
            var Q24;
            Q24=makeQuery(id+"F15.imprint","IMPRINT",FACE,{"disambiguationData":[TD([[makeQuery(id+"F15.imprint","IMPRINT",EDGE,{"derivedFrom":sQuery(id+"F15.wireOp",EDGE,"E48.1.25.0")}),1.0]])]});
            var Q25;
            Q25=makeQuery(id+"F15.imprint","IMPRINT",FACE,{"disambiguationData":[TD([[makeQuery(id+"F15.imprint","IMPRINT",EDGE,{"derivedFrom":sQuery(id+"F15.wireOp",EDGE,"E48.1.26.0")}),1.0]])]});
            var Q26;
            Q26=makeQuery(id+"F15.imprint","IMPRINT",FACE,{"disambiguationData":[TD([[makeQuery(id+"F15.imprint","IMPRINT",EDGE,{"derivedFrom":sQuery(id+"F15.wireOp",EDGE,"E48.1.27.0")}),1.0]])]});
            var Q27;
            Q27=makeQuery(id+"F15.imprint","IMPRINT",FACE,{"disambiguationData":[TD([[makeQuery(id+"F15.imprint","IMPRINT",EDGE,{"derivedFrom":sQuery(id+"F15.wireOp",EDGE,"E48.1.28.0")}),1.0]])]});
            var Q28;
            Q28=makeQuery(id+"F15.imprint","IMPRINT",FACE,{"disambiguationData":[TD([[makeQuery(id+"F15.imprint","IMPRINT",EDGE,{"derivedFrom":sQuery(id+"F15.wireOp",EDGE,"E48.1.29.0")}),1.0]])]});
            var Q29;
            Q29=makeQuery(id+"F15.imprint","IMPRINT",FACE,{"disambiguationData":[TD([[makeQuery(id+"F15.imprint","IMPRINT",EDGE,{"derivedFrom":sQuery(id+"F15.wireOp",EDGE,"E49.1.30.0")}),1.0]])]});
            var Q30;
            Q30=makeQuery(id+"F15.imprint","IMPRINT",FACE,{"disambiguationData":[TD([[makeQuery(id+"F15.imprint","IMPRINT",EDGE,{"derivedFrom":sQuery(id+"F15.wireOp",EDGE,"E49.1.33.0")}),1.0]])]});
            var Q31;
            Q31=makeQuery(id+"F15.imprint","IMPRINT",FACE,{"disambiguationData":[TD([[makeQuery(id+"F15.imprint","IMPRINT",EDGE,{"derivedFrom":sQuery(id+"F15.wireOp",EDGE,"E49.1.34.0")}),1.0]])]});
            var Q32;
            Q32=makeQuery(id+"F15.imprint","IMPRINT",FACE,{"disambiguationData":[TD([[makeQuery(id+"F15.imprint","IMPRINT",EDGE,{"derivedFrom":sQuery(id+"F15.wireOp",EDGE,"E49.1.35.0")}),1.0]])]});
            var Q33;
            Q33=makeQuery(id+"F15.imprint","IMPRINT",FACE,{"disambiguationData":[TD([[makeQuery(id+"F15.imprint","IMPRINT",EDGE,{"derivedFrom":sQuery(id+"F15.wireOp",EDGE,"E48.1.23.0")}),1.0]])]});
            var Q34;
            Q34=makeQuery(id+"F15.imprint","IMPRINT",FACE,{"disambiguationData":[TD([[makeQuery(id+"F15.imprint","IMPRINT",EDGE,{"derivedFrom":sQuery(id+"F15.wireOp",EDGE,"E48.1.22.0")}),1.0]])]});
            var Q35;
            Q35=makeQuery(id+"F15.imprint","IMPRINT",FACE,{"disambiguationData":[TD([[makeQuery(id+"F15.imprint","IMPRINT",EDGE,{"derivedFrom":sQuery(id+"F15.wireOp",EDGE,"E49.1.36.0")}),1.0]])]});
            var Q36;
            Q36=makeQuery(id+"F15.imprint","IMPRINT",FACE,{"disambiguationData":[TD([[makeQuery(id+"F15.imprint","IMPRINT",EDGE,{"derivedFrom":sQuery(id+"F15.wireOp",EDGE,"E49.1.37.0")}),1.0]])]});
            var Q37;
            Q37=makeQuery(id+"F15.imprint","IMPRINT",FACE,{"disambiguationData":[TD([[makeQuery(id+"F15.imprint","IMPRINT",EDGE,{"derivedFrom":sQuery(id+"F15.wireOp",EDGE,"E49.1.38.0")}),1.0]])]});
            var Q38;
            Q38=makeQuery(id+"F15.imprint","IMPRINT",FACE,{"disambiguationData":[TD([[makeQuery(id+"F15.imprint","IMPRINT",EDGE,{"derivedFrom":sQuery(id+"F15.wireOp",EDGE,"E49.1.32.0")}),1.0]])]});
            var Q39;
            Q39=makeQuery(id+"F15.imprint","IMPRINT",FACE,{"disambiguationData":[TD([[makeQuery(id+"F15.imprint","IMPRINT",EDGE,{"derivedFrom":sQuery(id+"F15.wireOp",EDGE,"E49.1.31.0")}),1.0]])]});
            extrude(context, id + "F16", {"entities" : qUnion([Q0, Q1, Q2, Q3, Q4, Q5, Q6, Q7, Q8, Q9, Q10, Q11, Q12, Q13, Q14, Q15, Q16, Q17, Q18, Q19, Q20, Q21, Q22, Q23, Q24, Q25, Q26, Q27, Q28, Q29, Q30, Q31, Q32, Q33, Q34, Q35, Q36, Q37, Q38, Q39]), "operationType" : NewBodyOperationType.REMOVE, "depth" : 25 * mm, "offsetDistance" : 25 * mm});
        }
        {
            var Q0;
            {var subQ0=sQuery(id+"F0.wireOp",EDGE,"E17");Q0=makeQuery(id+"F16.boolean.opBoolean","INTERSECT",EDGE,{"derivedFrom":[makeQuery(id+"F9.opFillet","BLEND_FACE",FACE,{"disambiguationData":[OSD([subQ0]),TDD([makeQuery(id+"F8.opExtrude","CAP_EDGE",EDGE,{"disambiguationData":[OSD([subQ0])],"isStart":true})])]}),makeQuery(id+"F16.opExtrude","SWEPT_FACE",FACE,{"disambiguationData":[OSD([sQuery(id+"F15.wireOp",EDGE,"E47.6.0")])]})]});}
            var Q1;
            {var subQ0=sQuery(id+"F0.wireOp",EDGE,"E17");Q1=makeQuery(id+"F16.boolean.opBoolean","INTERSECT",EDGE,{"derivedFrom":[makeQuery(id+"F9.opFillet","BLEND_FACE",FACE,{"disambiguationData":[OSD([subQ0]),TDD([makeQuery(id+"F8.opExtrude","CAP_EDGE",EDGE,{"disambiguationData":[OSD([subQ0])],"isStart":true})])]}),makeQuery(id+"F16.opExtrude","SWEPT_FACE",FACE,{"disambiguationData":[OSD([sQuery(id+"F15.wireOp",EDGE,"E47.7.0")])]})]});}
            var Q2;
            {var subQ0=sQuery(id+"F0.wireOp",EDGE,"E17");Q2=makeQuery(id+"F16.boolean.opBoolean","INTERSECT",EDGE,{"derivedFrom":[makeQuery(id+"F9.opFillet","BLEND_FACE",FACE,{"disambiguationData":[OSD([subQ0]),TDD([makeQuery(id+"F8.opExtrude","CAP_EDGE",EDGE,{"disambiguationData":[OSD([subQ0])],"isStart":true})])]}),makeQuery(id+"F16.opExtrude","SWEPT_FACE",FACE,{"disambiguationData":[OSD([sQuery(id+"F15.wireOp",EDGE,"E47.8.0")])]})]});}
            var Q3;
            {var subQ0=sQuery(id+"F0.wireOp",EDGE,"E17");Q3=makeQuery(id+"F16.boolean.opBoolean","INTERSECT",EDGE,{"derivedFrom":[makeQuery(id+"F9.opFillet","BLEND_FACE",FACE,{"disambiguationData":[OSD([subQ0]),TDD([makeQuery(id+"F8.opExtrude","CAP_EDGE",EDGE,{"disambiguationData":[OSD([subQ0])],"isStart":true})])]}),makeQuery(id+"F16.opExtrude","SWEPT_FACE",FACE,{"disambiguationData":[OSD([sQuery(id+"F15.wireOp",EDGE,"E47.9.0")])]})]});}
            var Q4;
            {var subQ0=sQuery(id+"F0.wireOp",EDGE,"E17");Q4=makeQuery(id+"F16.boolean.opBoolean","INTERSECT",EDGE,{"derivedFrom":[makeQuery(id+"F9.opFillet","BLEND_FACE",FACE,{"disambiguationData":[OSD([subQ0]),TDD([makeQuery(id+"F8.opExtrude","CAP_EDGE",EDGE,{"disambiguationData":[OSD([subQ0])],"isStart":true})])]}),makeQuery(id+"F16.opExtrude","SWEPT_FACE",FACE,{"disambiguationData":[OSD([sQuery(id+"F15.wireOp",EDGE,"E47.10.0")])]})]});}
            var Q5;
            {var subQ0=sQuery(id+"F0.wireOp",EDGE,"E17");Q5=makeQuery(id+"F16.boolean.opBoolean","INTERSECT",EDGE,{"derivedFrom":[makeQuery(id+"F9.opFillet","BLEND_FACE",FACE,{"disambiguationData":[OSD([subQ0]),TDD([makeQuery(id+"F8.opExtrude","CAP_EDGE",EDGE,{"disambiguationData":[OSD([subQ0])],"isStart":true})])]}),makeQuery(id+"F16.opExtrude","SWEPT_FACE",FACE,{"disambiguationData":[OSD([sQuery(id+"F15.wireOp",EDGE,"E47.12.0")])]})]});}
            var Q6;
            {var subQ0=sQuery(id+"F0.wireOp",EDGE,"E17");Q6=makeQuery(id+"F16.boolean.opBoolean","INTERSECT",EDGE,{"derivedFrom":[makeQuery(id+"F9.opFillet","BLEND_FACE",FACE,{"disambiguationData":[OSD([subQ0]),TDD([makeQuery(id+"F8.opExtrude","CAP_EDGE",EDGE,{"disambiguationData":[OSD([subQ0])],"isStart":true})])]}),makeQuery(id+"F16.opExtrude","SWEPT_FACE",FACE,{"disambiguationData":[OSD([sQuery(id+"F15.wireOp",EDGE,"E47.13.0")])]})]});}
            var Q7;
            {var subQ0=sQuery(id+"F0.wireOp",EDGE,"E17");Q7=makeQuery(id+"F16.boolean.opBoolean","INTERSECT",EDGE,{"derivedFrom":[makeQuery(id+"F9.opFillet","BLEND_FACE",FACE,{"disambiguationData":[OSD([subQ0]),TDD([makeQuery(id+"F8.opExtrude","CAP_EDGE",EDGE,{"disambiguationData":[OSD([subQ0])],"isStart":true})])]}),makeQuery(id+"F16.opExtrude","SWEPT_FACE",FACE,{"disambiguationData":[OSD([sQuery(id+"F15.wireOp",EDGE,"E47.14.0")])]})]});}
            var Q8;
            {var subQ0=sQuery(id+"F0.wireOp",EDGE,"E17");Q8=makeQuery(id+"F16.boolean.opBoolean","INTERSECT",EDGE,{"derivedFrom":[makeQuery(id+"F9.opFillet","BLEND_FACE",FACE,{"disambiguationData":[OSD([subQ0]),TDD([makeQuery(id+"F8.opExtrude","CAP_EDGE",EDGE,{"disambiguationData":[OSD([subQ0])],"isStart":true})])]}),makeQuery(id+"F16.opExtrude","SWEPT_FACE",FACE,{"disambiguationData":[OSD([sQuery(id+"F15.wireOp",EDGE,"E47.15.0")])]})]});}
            var Q9;
            {var subQ0=sQuery(id+"F0.wireOp",EDGE,"E17");Q9=makeQuery(id+"F16.boolean.opBoolean","INTERSECT",EDGE,{"derivedFrom":[makeQuery(id+"F9.opFillet","BLEND_FACE",FACE,{"disambiguationData":[OSD([subQ0]),TDD([makeQuery(id+"F8.opExtrude","CAP_EDGE",EDGE,{"disambiguationData":[OSD([subQ0])],"isStart":true})])]}),makeQuery(id+"F16.opExtrude","SWEPT_FACE",FACE,{"disambiguationData":[OSD([sQuery(id+"F15.wireOp",EDGE,"E47.16.0")])]})]});}
            var Q10;
            {var subQ0=sQuery(id+"F0.wireOp",EDGE,"E17");Q10=makeQuery(id+"F16.boolean.opBoolean","INTERSECT",EDGE,{"derivedFrom":[makeQuery(id+"F9.opFillet","BLEND_FACE",FACE,{"disambiguationData":[OSD([subQ0]),TDD([makeQuery(id+"F8.opExtrude","CAP_EDGE",EDGE,{"disambiguationData":[OSD([subQ0])],"isStart":true})])]}),makeQuery(id+"F16.opExtrude","SWEPT_FACE",FACE,{"disambiguationData":[OSD([sQuery(id+"F15.wireOp",EDGE,"E47.17.0")])]})]});}
            var Q11;
            {var subQ0=sQuery(id+"F0.wireOp",EDGE,"E17");Q11=makeQuery(id+"F16.boolean.opBoolean","INTERSECT",EDGE,{"derivedFrom":[makeQuery(id+"F9.opFillet","BLEND_FACE",FACE,{"disambiguationData":[OSD([subQ0]),TDD([makeQuery(id+"F8.opExtrude","CAP_EDGE",EDGE,{"disambiguationData":[OSD([subQ0])],"isStart":true})])]}),makeQuery(id+"F16.opExtrude","SWEPT_FACE",FACE,{"disambiguationData":[OSD([sQuery(id+"F15.wireOp",EDGE,"E47.19.0")])]})]});}
            var Q12;
            {var subQ0=sQuery(id+"F0.wireOp",EDGE,"E17");Q12=makeQuery(id+"F16.boolean.opBoolean","INTERSECT",EDGE,{"derivedFrom":[makeQuery(id+"F9.opFillet","BLEND_FACE",FACE,{"disambiguationData":[OSD([subQ0]),TDD([makeQuery(id+"F8.opExtrude","CAP_EDGE",EDGE,{"disambiguationData":[OSD([subQ0])],"isStart":true})])]}),makeQuery(id+"F16.opExtrude","SWEPT_FACE",FACE,{"disambiguationData":[OSD([sQuery(id+"F15.wireOp",EDGE,"E48.1.20.0")])]})]});}
            var Q13;
            {var subQ0=sQuery(id+"F0.wireOp",EDGE,"E17");Q13=makeQuery(id+"F16.boolean.opBoolean","INTERSECT",EDGE,{"derivedFrom":[makeQuery(id+"F9.opFillet","BLEND_FACE",FACE,{"disambiguationData":[OSD([subQ0]),TDD([makeQuery(id+"F8.opExtrude","CAP_EDGE",EDGE,{"disambiguationData":[OSD([subQ0])],"isStart":true})])]}),makeQuery(id+"F16.opExtrude","SWEPT_FACE",FACE,{"disambiguationData":[OSD([sQuery(id+"F15.wireOp",EDGE,"E48.1.21.0")])]})]});}
            var Q14;
            {var subQ0=sQuery(id+"F0.wireOp",EDGE,"E17");Q14=makeQuery(id+"F16.boolean.opBoolean","INTERSECT",EDGE,{"derivedFrom":[makeQuery(id+"F9.opFillet","BLEND_FACE",FACE,{"disambiguationData":[OSD([subQ0]),TDD([makeQuery(id+"F8.opExtrude","CAP_EDGE",EDGE,{"disambiguationData":[OSD([subQ0])],"isStart":true})])]}),makeQuery(id+"F16.opExtrude","SWEPT_FACE",FACE,{"disambiguationData":[OSD([sQuery(id+"F15.wireOp",EDGE,"E48.1.22.0")])]})]});}
            var Q15;
            {var subQ0=sQuery(id+"F0.wireOp",EDGE,"E17");Q15=makeQuery(id+"F16.boolean.opBoolean","INTERSECT",EDGE,{"derivedFrom":[makeQuery(id+"F9.opFillet","BLEND_FACE",FACE,{"disambiguationData":[OSD([subQ0]),TDD([makeQuery(id+"F8.opExtrude","CAP_EDGE",EDGE,{"disambiguationData":[OSD([subQ0])],"isStart":true})])]}),makeQuery(id+"F16.opExtrude","SWEPT_FACE",FACE,{"disambiguationData":[OSD([sQuery(id+"F15.wireOp",EDGE,"E47.18.0")])]})]});}
            var Q16;
            {var subQ0=sQuery(id+"F0.wireOp",EDGE,"E17");Q16=makeQuery(id+"F16.boolean.opBoolean","INTERSECT",EDGE,{"derivedFrom":[makeQuery(id+"F9.opFillet","BLEND_FACE",FACE,{"disambiguationData":[OSD([subQ0]),TDD([makeQuery(id+"F8.opExtrude","CAP_EDGE",EDGE,{"disambiguationData":[OSD([subQ0])],"isStart":true})])]}),makeQuery(id+"F16.opExtrude","SWEPT_FACE",FACE,{"disambiguationData":[OSD([sQuery(id+"F15.wireOp",EDGE,"E48.1.23.0")])]})]});}
            var Q17;
            {var subQ0=sQuery(id+"F0.wireOp",EDGE,"E17");Q17=makeQuery(id+"F16.boolean.opBoolean","INTERSECT",EDGE,{"derivedFrom":[makeQuery(id+"F9.opFillet","BLEND_FACE",FACE,{"disambiguationData":[OSD([subQ0]),TDD([makeQuery(id+"F8.opExtrude","CAP_EDGE",EDGE,{"disambiguationData":[OSD([subQ0])],"isStart":true})])]}),makeQuery(id+"F16.opExtrude","SWEPT_FACE",FACE,{"disambiguationData":[OSD([sQuery(id+"F15.wireOp",EDGE,"E48.1.25.0")])]})]});}
            var Q18;
            {var subQ0=sQuery(id+"F0.wireOp",EDGE,"E17");Q18=makeQuery(id+"F16.boolean.opBoolean","INTERSECT",EDGE,{"derivedFrom":[makeQuery(id+"F9.opFillet","BLEND_FACE",FACE,{"disambiguationData":[OSD([subQ0]),TDD([makeQuery(id+"F8.opExtrude","CAP_EDGE",EDGE,{"disambiguationData":[OSD([subQ0])],"isStart":true})])]}),makeQuery(id+"F16.opExtrude","SWEPT_FACE",FACE,{"disambiguationData":[OSD([sQuery(id+"F15.wireOp",EDGE,"E48.1.26.0")])]})]});}
            var Q19;
            {var subQ0=sQuery(id+"F0.wireOp",EDGE,"E17");Q19=makeQuery(id+"F16.boolean.opBoolean","INTERSECT",EDGE,{"derivedFrom":[makeQuery(id+"F9.opFillet","BLEND_FACE",FACE,{"disambiguationData":[OSD([subQ0]),TDD([makeQuery(id+"F8.opExtrude","CAP_EDGE",EDGE,{"disambiguationData":[OSD([subQ0])],"isStart":true})])]}),makeQuery(id+"F16.opExtrude","SWEPT_FACE",FACE,{"disambiguationData":[OSD([sQuery(id+"F15.wireOp",EDGE,"E48.1.27.0")])]})]});}
            var Q20;
            {var subQ0=sQuery(id+"F0.wireOp",EDGE,"E17");Q20=makeQuery(id+"F16.boolean.opBoolean","INTERSECT",EDGE,{"derivedFrom":[makeQuery(id+"F9.opFillet","BLEND_FACE",FACE,{"disambiguationData":[OSD([subQ0]),TDD([makeQuery(id+"F8.opExtrude","CAP_EDGE",EDGE,{"disambiguationData":[OSD([subQ0])],"isStart":true})])]}),makeQuery(id+"F16.opExtrude","SWEPT_FACE",FACE,{"disambiguationData":[OSD([sQuery(id+"F15.wireOp",EDGE,"E48.1.28.0")])]})]});}
            var Q21;
            {var subQ0=sQuery(id+"F0.wireOp",EDGE,"E17");Q21=makeQuery(id+"F16.boolean.opBoolean","INTERSECT",EDGE,{"derivedFrom":[makeQuery(id+"F9.opFillet","BLEND_FACE",FACE,{"disambiguationData":[OSD([subQ0]),TDD([makeQuery(id+"F8.opExtrude","CAP_EDGE",EDGE,{"disambiguationData":[OSD([subQ0])],"isStart":true})])]}),makeQuery(id+"F16.opExtrude","SWEPT_FACE",FACE,{"disambiguationData":[OSD([sQuery(id+"F15.wireOp",EDGE,"E48.1.29.0")])]})]});}
            var Q22;
            {var subQ0=sQuery(id+"F0.wireOp",EDGE,"E17");Q22=makeQuery(id+"F16.boolean.opBoolean","INTERSECT",EDGE,{"derivedFrom":[makeQuery(id+"F9.opFillet","BLEND_FACE",FACE,{"disambiguationData":[OSD([subQ0]),TDD([makeQuery(id+"F8.opExtrude","CAP_EDGE",EDGE,{"disambiguationData":[OSD([subQ0])],"isStart":true})])]}),makeQuery(id+"F16.opExtrude","SWEPT_FACE",FACE,{"disambiguationData":[OSD([sQuery(id+"F15.wireOp",EDGE,"E49.1.30.0")])]})]});}
            var Q23;
            {var subQ0=sQuery(id+"F0.wireOp",EDGE,"E17");Q23=makeQuery(id+"F16.boolean.opBoolean","INTERSECT",EDGE,{"derivedFrom":[makeQuery(id+"F9.opFillet","BLEND_FACE",FACE,{"disambiguationData":[OSD([subQ0]),TDD([makeQuery(id+"F8.opExtrude","CAP_EDGE",EDGE,{"disambiguationData":[OSD([subQ0])],"isStart":true})])]}),makeQuery(id+"F16.opExtrude","SWEPT_FACE",FACE,{"disambiguationData":[OSD([sQuery(id+"F15.wireOp",EDGE,"E49.1.31.0")])]})]});}
            var Q24;
            {var subQ0=sQuery(id+"F0.wireOp",EDGE,"E17");Q24=makeQuery(id+"F16.boolean.opBoolean","INTERSECT",EDGE,{"derivedFrom":[makeQuery(id+"F9.opFillet","BLEND_FACE",FACE,{"disambiguationData":[OSD([subQ0]),TDD([makeQuery(id+"F8.opExtrude","CAP_EDGE",EDGE,{"disambiguationData":[OSD([subQ0])],"isStart":true})])]}),makeQuery(id+"F16.opExtrude","SWEPT_FACE",FACE,{"disambiguationData":[OSD([sQuery(id+"F15.wireOp",EDGE,"E49.1.32.0")])]})]});}
            var Q25;
            {var subQ0=sQuery(id+"F0.wireOp",EDGE,"E17");Q25=makeQuery(id+"F16.boolean.opBoolean","INTERSECT",EDGE,{"derivedFrom":[makeQuery(id+"F9.opFillet","BLEND_FACE",FACE,{"disambiguationData":[OSD([subQ0]),TDD([makeQuery(id+"F8.opExtrude","CAP_EDGE",EDGE,{"disambiguationData":[OSD([subQ0])],"isStart":true})])]}),makeQuery(id+"F16.opExtrude","SWEPT_FACE",FACE,{"disambiguationData":[OSD([sQuery(id+"F15.wireOp",EDGE,"E49.1.33.0")])]})]});}
            var Q26;
            {var subQ0=sQuery(id+"F0.wireOp",EDGE,"E17");Q26=makeQuery(id+"F16.boolean.opBoolean","INTERSECT",EDGE,{"derivedFrom":[makeQuery(id+"F9.opFillet","BLEND_FACE",FACE,{"disambiguationData":[OSD([subQ0]),TDD([makeQuery(id+"F8.opExtrude","CAP_EDGE",EDGE,{"disambiguationData":[OSD([subQ0])],"isStart":true})])]}),makeQuery(id+"F16.opExtrude","SWEPT_FACE",FACE,{"disambiguationData":[OSD([sQuery(id+"F15.wireOp",EDGE,"E49.1.34.0")])]})]});}
            var Q27;
            {var subQ0=sQuery(id+"F0.wireOp",EDGE,"E17");Q27=makeQuery(id+"F16.boolean.opBoolean","INTERSECT",EDGE,{"derivedFrom":[makeQuery(id+"F9.opFillet","BLEND_FACE",FACE,{"disambiguationData":[OSD([subQ0]),TDD([makeQuery(id+"F8.opExtrude","CAP_EDGE",EDGE,{"disambiguationData":[OSD([subQ0])],"isStart":true})])]}),makeQuery(id+"F16.opExtrude","SWEPT_FACE",FACE,{"disambiguationData":[OSD([sQuery(id+"F15.wireOp",EDGE,"E48.1.24.0")])]})]});}
            var Q28;
            {var subQ0=sQuery(id+"F0.wireOp",EDGE,"E17");Q28=makeQuery(id+"F16.boolean.opBoolean","INTERSECT",EDGE,{"derivedFrom":[makeQuery(id+"F9.opFillet","BLEND_FACE",FACE,{"disambiguationData":[OSD([subQ0]),TDD([makeQuery(id+"F8.opExtrude","CAP_EDGE",EDGE,{"disambiguationData":[OSD([subQ0])],"isStart":true})])]}),makeQuery(id+"F16.opExtrude","SWEPT_FACE",FACE,{"disambiguationData":[OSD([sQuery(id+"F15.wireOp",EDGE,"E49.1.35.0")])]})]});}
            var Q29;
            {var subQ0=sQuery(id+"F0.wireOp",EDGE,"E17");Q29=makeQuery(id+"F16.boolean.opBoolean","INTERSECT",EDGE,{"derivedFrom":[makeQuery(id+"F9.opFillet","BLEND_FACE",FACE,{"disambiguationData":[OSD([subQ0]),TDD([makeQuery(id+"F8.opExtrude","CAP_EDGE",EDGE,{"disambiguationData":[OSD([subQ0])],"isStart":true})])]}),makeQuery(id+"F16.opExtrude","SWEPT_FACE",FACE,{"disambiguationData":[OSD([sQuery(id+"F15.wireOp",EDGE,"E47.11.0")])]})]});}
            var Q30;
            {var subQ0=sQuery(id+"F0.wireOp",EDGE,"E17");Q30=makeQuery(id+"F16.boolean.opBoolean","INTERSECT",EDGE,{"derivedFrom":[makeQuery(id+"F9.opFillet","BLEND_FACE",FACE,{"disambiguationData":[OSD([subQ0]),TDD([makeQuery(id+"F8.opExtrude","CAP_EDGE",EDGE,{"disambiguationData":[OSD([subQ0])],"isStart":true})])]}),makeQuery(id+"F16.opExtrude","SWEPT_FACE",FACE,{"disambiguationData":[OSD([sQuery(id+"F15.wireOp",EDGE,"E47.5.0")])]})]});}
            var Q31;
            {var subQ0=sQuery(id+"F0.wireOp",EDGE,"E17");Q31=makeQuery(id+"F16.boolean.opBoolean","INTERSECT",EDGE,{"derivedFrom":[makeQuery(id+"F9.opFillet","BLEND_FACE",FACE,{"disambiguationData":[OSD([subQ0]),TDD([makeQuery(id+"F8.opExtrude","CAP_EDGE",EDGE,{"disambiguationData":[OSD([subQ0])],"isStart":true})])]}),makeQuery(id+"F16.opExtrude","SWEPT_FACE",FACE,{"disambiguationData":[OSD([sQuery(id+"F15.wireOp",EDGE,"E47.4.0")])]})]});}
            var Q32;
            {var subQ0=sQuery(id+"F0.wireOp",EDGE,"E17");Q32=makeQuery(id+"F16.boolean.opBoolean","INTERSECT",EDGE,{"derivedFrom":[makeQuery(id+"F9.opFillet","BLEND_FACE",FACE,{"disambiguationData":[OSD([subQ0]),TDD([makeQuery(id+"F8.opExtrude","CAP_EDGE",EDGE,{"disambiguationData":[OSD([subQ0])],"isStart":true})])]}),makeQuery(id+"F16.opExtrude","SWEPT_FACE",FACE,{"disambiguationData":[OSD([sQuery(id+"F15.wireOp",EDGE,"E47.3.0")])]})]});}
            var Q33;
            {var subQ0=sQuery(id+"F0.wireOp",EDGE,"E17");Q33=makeQuery(id+"F16.boolean.opBoolean","INTERSECT",EDGE,{"derivedFrom":[makeQuery(id+"F9.opFillet","BLEND_FACE",FACE,{"disambiguationData":[OSD([subQ0]),TDD([makeQuery(id+"F8.opExtrude","CAP_EDGE",EDGE,{"disambiguationData":[OSD([subQ0])],"isStart":true})])]}),makeQuery(id+"F16.opExtrude","SWEPT_FACE",FACE,{"disambiguationData":[OSD([sQuery(id+"F15.wireOp",EDGE,"E47.2.0")])]})]});}
            var Q34;
            {var subQ0=sQuery(id+"F0.wireOp",EDGE,"E17");Q34=makeQuery(id+"F16.boolean.opBoolean","INTERSECT",EDGE,{"derivedFrom":[makeQuery(id+"F9.opFillet","BLEND_FACE",FACE,{"disambiguationData":[OSD([subQ0]),TDD([makeQuery(id+"F8.opExtrude","CAP_EDGE",EDGE,{"disambiguationData":[OSD([subQ0])],"isStart":true})])]}),makeQuery(id+"F16.opExtrude","SWEPT_FACE",FACE,{"disambiguationData":[OSD([sQuery(id+"F15.wireOp",EDGE,"E47.1.0")])]})]});}
            var Q35;
            {var subQ0=sQuery(id+"F0.wireOp",EDGE,"E17");Q35=makeQuery(id+"F16.boolean.opBoolean","INTERSECT",EDGE,{"derivedFrom":[makeQuery(id+"F9.opFillet","BLEND_FACE",FACE,{"disambiguationData":[OSD([subQ0]),TDD([makeQuery(id+"F8.opExtrude","CAP_EDGE",EDGE,{"disambiguationData":[OSD([subQ0])],"isStart":true})])]}),makeQuery(id+"F16.opExtrude","SWEPT_FACE",FACE,{"disambiguationData":[OSD([sQuery(id+"F15.wireOp",EDGE,"E46")])]})]});}
            var Q36;
            {var subQ0=sQuery(id+"F0.wireOp",EDGE,"E17");Q36=makeQuery(id+"F16.boolean.opBoolean","INTERSECT",EDGE,{"derivedFrom":[makeQuery(id+"F9.opFillet","BLEND_FACE",FACE,{"disambiguationData":[OSD([subQ0]),TDD([makeQuery(id+"F8.opExtrude","CAP_EDGE",EDGE,{"disambiguationData":[OSD([subQ0])],"isStart":true})])]}),makeQuery(id+"F16.opExtrude","SWEPT_FACE",FACE,{"disambiguationData":[OSD([sQuery(id+"F15.wireOp",EDGE,"E49.1.39.0")])]})]});}
            var Q37;
            {var subQ0=sQuery(id+"F0.wireOp",EDGE,"E17");Q37=makeQuery(id+"F16.boolean.opBoolean","INTERSECT",EDGE,{"derivedFrom":[makeQuery(id+"F9.opFillet","BLEND_FACE",FACE,{"disambiguationData":[OSD([subQ0]),TDD([makeQuery(id+"F8.opExtrude","CAP_EDGE",EDGE,{"disambiguationData":[OSD([subQ0])],"isStart":true})])]}),makeQuery(id+"F16.opExtrude","SWEPT_FACE",FACE,{"disambiguationData":[OSD([sQuery(id+"F15.wireOp",EDGE,"E49.1.38.0")])]})]});}
            var Q38;
            {var subQ0=sQuery(id+"F0.wireOp",EDGE,"E17");Q38=makeQuery(id+"F16.boolean.opBoolean","INTERSECT",EDGE,{"derivedFrom":[makeQuery(id+"F9.opFillet","BLEND_FACE",FACE,{"disambiguationData":[OSD([subQ0]),TDD([makeQuery(id+"F8.opExtrude","CAP_EDGE",EDGE,{"disambiguationData":[OSD([subQ0])],"isStart":true})])]}),makeQuery(id+"F16.opExtrude","SWEPT_FACE",FACE,{"disambiguationData":[OSD([sQuery(id+"F15.wireOp",EDGE,"E49.1.37.0")])]})]});}
            var Q39;
            {var subQ0=sQuery(id+"F0.wireOp",EDGE,"E17");Q39=makeQuery(id+"F16.boolean.opBoolean","INTERSECT",EDGE,{"derivedFrom":[makeQuery(id+"F9.opFillet","BLEND_FACE",FACE,{"disambiguationData":[OSD([subQ0]),TDD([makeQuery(id+"F8.opExtrude","CAP_EDGE",EDGE,{"disambiguationData":[OSD([subQ0])],"isStart":true})])]}),makeQuery(id+"F16.opExtrude","SWEPT_FACE",FACE,{"disambiguationData":[OSD([sQuery(id+"F15.wireOp",EDGE,"E49.1.36.0")])]})]});}
            fillet(context, id + "F17", {"entities" : qUnion([Q0, Q1, Q2, Q3, Q4, Q5, Q6, Q7, Q8, Q9, Q10, Q11, Q12, Q13, Q14, Q15, Q16, Q17, Q18, Q19, Q20, Q21, Q22, Q23, Q24, Q25, Q26, Q27, Q28, Q29, Q30, Q31, Q32, Q33, Q34, Q35, Q36, Q37, Q38, Q39]), "tangentPropagation" : true, "radius" : .8 * mm, "defaultsChanged" : true, "vertexSettings" : [], "allowEdgeOverflow" : false});
        }
        {
            var Q0;
            {var subQ0=sQuery(id+"F0.wireOp",EDGE,"E17");Q0=makeQuery(id+"F16.boolean.opBoolean","INTERSECT",EDGE,{"derivedFrom":[makeQuery(id+"F9.opFillet","BLEND_FACE",FACE,{"disambiguationData":[OSD([subQ0]),TDD([makeQuery(id+"F8.opExtrude","CAP_EDGE",EDGE,{"disambiguationData":[OSD([subQ0])],"isStart":false})])]}),makeQuery(id+"F16.opExtrude","SWEPT_FACE",FACE,{"disambiguationData":[OSD([sQuery(id+"F15.wireOp",EDGE,"E47.18.0")])]})]});}
            var Q1;
            {var subQ0=sQuery(id+"F0.wireOp",EDGE,"E17");Q1=makeQuery(id+"F16.boolean.opBoolean","INTERSECT",EDGE,{"derivedFrom":[makeQuery(id+"F9.opFillet","BLEND_FACE",FACE,{"disambiguationData":[OSD([subQ0]),TDD([makeQuery(id+"F8.opExtrude","CAP_EDGE",EDGE,{"disambiguationData":[OSD([subQ0])],"isStart":false})])]}),makeQuery(id+"F16.opExtrude","SWEPT_FACE",FACE,{"disambiguationData":[OSD([sQuery(id+"F15.wireOp",EDGE,"E47.19.0")])]})]});}
            var Q2;
            {var subQ0=sQuery(id+"F0.wireOp",EDGE,"E17");Q2=makeQuery(id+"F16.boolean.opBoolean","INTERSECT",EDGE,{"derivedFrom":[makeQuery(id+"F9.opFillet","BLEND_FACE",FACE,{"disambiguationData":[OSD([subQ0]),TDD([makeQuery(id+"F8.opExtrude","CAP_EDGE",EDGE,{"disambiguationData":[OSD([subQ0])],"isStart":false})])]}),makeQuery(id+"F16.opExtrude","SWEPT_FACE",FACE,{"disambiguationData":[OSD([sQuery(id+"F15.wireOp",EDGE,"E48.1.20.0")])]})]});}
            var Q3;
            {var subQ0=sQuery(id+"F0.wireOp",EDGE,"E17");Q3=makeQuery(id+"F16.boolean.opBoolean","INTERSECT",EDGE,{"derivedFrom":[makeQuery(id+"F9.opFillet","BLEND_FACE",FACE,{"disambiguationData":[OSD([subQ0]),TDD([makeQuery(id+"F8.opExtrude","CAP_EDGE",EDGE,{"disambiguationData":[OSD([subQ0])],"isStart":false})])]}),makeQuery(id+"F16.opExtrude","SWEPT_FACE",FACE,{"disambiguationData":[OSD([sQuery(id+"F15.wireOp",EDGE,"E48.1.21.0")])]})]});}
            var Q4;
            {var subQ0=sQuery(id+"F0.wireOp",EDGE,"E17");Q4=makeQuery(id+"F16.boolean.opBoolean","INTERSECT",EDGE,{"derivedFrom":[makeQuery(id+"F9.opFillet","BLEND_FACE",FACE,{"disambiguationData":[OSD([subQ0]),TDD([makeQuery(id+"F8.opExtrude","CAP_EDGE",EDGE,{"disambiguationData":[OSD([subQ0])],"isStart":false})])]}),makeQuery(id+"F16.opExtrude","SWEPT_FACE",FACE,{"disambiguationData":[OSD([sQuery(id+"F15.wireOp",EDGE,"E47.17.0")])]})]});}
            var Q5;
            {var subQ0=sQuery(id+"F0.wireOp",EDGE,"E17");Q5=makeQuery(id+"F16.boolean.opBoolean","INTERSECT",EDGE,{"derivedFrom":[makeQuery(id+"F9.opFillet","BLEND_FACE",FACE,{"disambiguationData":[OSD([subQ0]),TDD([makeQuery(id+"F8.opExtrude","CAP_EDGE",EDGE,{"disambiguationData":[OSD([subQ0])],"isStart":false})])]}),makeQuery(id+"F16.opExtrude","SWEPT_FACE",FACE,{"disambiguationData":[OSD([sQuery(id+"F15.wireOp",EDGE,"E47.16.0")])]})]});}
            var Q6;
            {var subQ0=sQuery(id+"F0.wireOp",EDGE,"E17");Q6=makeQuery(id+"F16.boolean.opBoolean","INTERSECT",EDGE,{"derivedFrom":[makeQuery(id+"F9.opFillet","BLEND_FACE",FACE,{"disambiguationData":[OSD([subQ0]),TDD([makeQuery(id+"F8.opExtrude","CAP_EDGE",EDGE,{"disambiguationData":[OSD([subQ0])],"isStart":false})])]}),makeQuery(id+"F16.opExtrude","SWEPT_FACE",FACE,{"disambiguationData":[OSD([sQuery(id+"F15.wireOp",EDGE,"E47.15.0")])]})]});}
            var Q7;
            {var subQ0=sQuery(id+"F0.wireOp",EDGE,"E17");Q7=makeQuery(id+"F16.boolean.opBoolean","INTERSECT",EDGE,{"derivedFrom":[makeQuery(id+"F9.opFillet","BLEND_FACE",FACE,{"disambiguationData":[OSD([subQ0]),TDD([makeQuery(id+"F8.opExtrude","CAP_EDGE",EDGE,{"disambiguationData":[OSD([subQ0])],"isStart":false})])]}),makeQuery(id+"F16.opExtrude","SWEPT_FACE",FACE,{"disambiguationData":[OSD([sQuery(id+"F15.wireOp",EDGE,"E47.14.0")])]})]});}
            var Q8;
            {var subQ0=sQuery(id+"F0.wireOp",EDGE,"E17");Q8=makeQuery(id+"F16.boolean.opBoolean","INTERSECT",EDGE,{"derivedFrom":[makeQuery(id+"F9.opFillet","BLEND_FACE",FACE,{"disambiguationData":[OSD([subQ0]),TDD([makeQuery(id+"F8.opExtrude","CAP_EDGE",EDGE,{"disambiguationData":[OSD([subQ0])],"isStart":false})])]}),makeQuery(id+"F16.opExtrude","SWEPT_FACE",FACE,{"disambiguationData":[OSD([sQuery(id+"F15.wireOp",EDGE,"E47.13.0")])]})]});}
            var Q9;
            {var subQ0=sQuery(id+"F0.wireOp",EDGE,"E17");Q9=makeQuery(id+"F16.boolean.opBoolean","INTERSECT",EDGE,{"derivedFrom":[makeQuery(id+"F9.opFillet","BLEND_FACE",FACE,{"disambiguationData":[OSD([subQ0]),TDD([makeQuery(id+"F8.opExtrude","CAP_EDGE",EDGE,{"disambiguationData":[OSD([subQ0])],"isStart":false})])]}),makeQuery(id+"F16.opExtrude","SWEPT_FACE",FACE,{"disambiguationData":[OSD([sQuery(id+"F15.wireOp",EDGE,"E47.12.0")])]})]});}
            var Q10;
            {var subQ0=sQuery(id+"F0.wireOp",EDGE,"E17");Q10=makeQuery(id+"F16.boolean.opBoolean","INTERSECT",EDGE,{"derivedFrom":[makeQuery(id+"F9.opFillet","BLEND_FACE",FACE,{"disambiguationData":[OSD([subQ0]),TDD([makeQuery(id+"F8.opExtrude","CAP_EDGE",EDGE,{"disambiguationData":[OSD([subQ0])],"isStart":false})])]}),makeQuery(id+"F16.opExtrude","SWEPT_FACE",FACE,{"disambiguationData":[OSD([sQuery(id+"F15.wireOp",EDGE,"E47.11.0")])]})]});}
            var Q11;
            {var subQ0=sQuery(id+"F0.wireOp",EDGE,"E17");Q11=makeQuery(id+"F16.boolean.opBoolean","INTERSECT",EDGE,{"derivedFrom":[makeQuery(id+"F9.opFillet","BLEND_FACE",FACE,{"disambiguationData":[OSD([subQ0]),TDD([makeQuery(id+"F8.opExtrude","CAP_EDGE",EDGE,{"disambiguationData":[OSD([subQ0])],"isStart":false})])]}),makeQuery(id+"F16.opExtrude","SWEPT_FACE",FACE,{"disambiguationData":[OSD([sQuery(id+"F15.wireOp",EDGE,"E47.10.0")])]})]});}
            var Q12;
            {var subQ0=sQuery(id+"F0.wireOp",EDGE,"E17");Q12=makeQuery(id+"F16.boolean.opBoolean","INTERSECT",EDGE,{"derivedFrom":[makeQuery(id+"F9.opFillet","BLEND_FACE",FACE,{"disambiguationData":[OSD([subQ0]),TDD([makeQuery(id+"F8.opExtrude","CAP_EDGE",EDGE,{"disambiguationData":[OSD([subQ0])],"isStart":false})])]}),makeQuery(id+"F16.opExtrude","SWEPT_FACE",FACE,{"disambiguationData":[OSD([sQuery(id+"F15.wireOp",EDGE,"E47.9.0")])]})]});}
            var Q13;
            {var subQ0=sQuery(id+"F0.wireOp",EDGE,"E17");Q13=makeQuery(id+"F16.boolean.opBoolean","INTERSECT",EDGE,{"derivedFrom":[makeQuery(id+"F9.opFillet","BLEND_FACE",FACE,{"disambiguationData":[OSD([subQ0]),TDD([makeQuery(id+"F8.opExtrude","CAP_EDGE",EDGE,{"disambiguationData":[OSD([subQ0])],"isStart":false})])]}),makeQuery(id+"F16.opExtrude","SWEPT_FACE",FACE,{"disambiguationData":[OSD([sQuery(id+"F15.wireOp",EDGE,"E47.8.0")])]})]});}
            var Q14;
            {var subQ0=sQuery(id+"F0.wireOp",EDGE,"E17");Q14=makeQuery(id+"F16.boolean.opBoolean","INTERSECT",EDGE,{"derivedFrom":[makeQuery(id+"F9.opFillet","BLEND_FACE",FACE,{"disambiguationData":[OSD([subQ0]),TDD([makeQuery(id+"F8.opExtrude","CAP_EDGE",EDGE,{"disambiguationData":[OSD([subQ0])],"isStart":false})])]}),makeQuery(id+"F16.opExtrude","SWEPT_FACE",FACE,{"disambiguationData":[OSD([sQuery(id+"F15.wireOp",EDGE,"E47.7.0")])]})]});}
            var Q15;
            {var subQ0=sQuery(id+"F0.wireOp",EDGE,"E17");Q15=makeQuery(id+"F16.boolean.opBoolean","INTERSECT",EDGE,{"derivedFrom":[makeQuery(id+"F9.opFillet","BLEND_FACE",FACE,{"disambiguationData":[OSD([subQ0]),TDD([makeQuery(id+"F8.opExtrude","CAP_EDGE",EDGE,{"disambiguationData":[OSD([subQ0])],"isStart":false})])]}),makeQuery(id+"F16.opExtrude","SWEPT_FACE",FACE,{"disambiguationData":[OSD([sQuery(id+"F15.wireOp",EDGE,"E47.6.0")])]})]});}
            var Q16;
            {var subQ0=sQuery(id+"F0.wireOp",EDGE,"E17");Q16=makeQuery(id+"F16.boolean.opBoolean","INTERSECT",EDGE,{"derivedFrom":[makeQuery(id+"F9.opFillet","BLEND_FACE",FACE,{"disambiguationData":[OSD([subQ0]),TDD([makeQuery(id+"F8.opExtrude","CAP_EDGE",EDGE,{"disambiguationData":[OSD([subQ0])],"isStart":false})])]}),makeQuery(id+"F16.opExtrude","SWEPT_FACE",FACE,{"disambiguationData":[OSD([sQuery(id+"F15.wireOp",EDGE,"E47.5.0")])]})]});}
            var Q17;
            {var subQ0=sQuery(id+"F0.wireOp",EDGE,"E17");Q17=makeQuery(id+"F16.boolean.opBoolean","INTERSECT",EDGE,{"derivedFrom":[makeQuery(id+"F9.opFillet","BLEND_FACE",FACE,{"disambiguationData":[OSD([subQ0]),TDD([makeQuery(id+"F8.opExtrude","CAP_EDGE",EDGE,{"disambiguationData":[OSD([subQ0])],"isStart":false})])]}),makeQuery(id+"F16.opExtrude","SWEPT_FACE",FACE,{"disambiguationData":[OSD([sQuery(id+"F15.wireOp",EDGE,"E47.4.0")])]})]});}
            var Q18;
            {var subQ0=sQuery(id+"F0.wireOp",EDGE,"E17");Q18=makeQuery(id+"F16.boolean.opBoolean","INTERSECT",EDGE,{"derivedFrom":[makeQuery(id+"F9.opFillet","BLEND_FACE",FACE,{"disambiguationData":[OSD([subQ0]),TDD([makeQuery(id+"F8.opExtrude","CAP_EDGE",EDGE,{"disambiguationData":[OSD([subQ0])],"isStart":false})])]}),makeQuery(id+"F16.opExtrude","SWEPT_FACE",FACE,{"disambiguationData":[OSD([sQuery(id+"F15.wireOp",EDGE,"E47.3.0")])]})]});}
            var Q19;
            {var subQ0=sQuery(id+"F0.wireOp",EDGE,"E17");Q19=makeQuery(id+"F16.boolean.opBoolean","INTERSECT",EDGE,{"derivedFrom":[makeQuery(id+"F9.opFillet","BLEND_FACE",FACE,{"disambiguationData":[OSD([subQ0]),TDD([makeQuery(id+"F8.opExtrude","CAP_EDGE",EDGE,{"disambiguationData":[OSD([subQ0])],"isStart":false})])]}),makeQuery(id+"F16.opExtrude","SWEPT_FACE",FACE,{"disambiguationData":[OSD([sQuery(id+"F15.wireOp",EDGE,"E47.2.0")])]})]});}
            var Q20;
            {var subQ0=sQuery(id+"F0.wireOp",EDGE,"E17");Q20=makeQuery(id+"F16.boolean.opBoolean","INTERSECT",EDGE,{"derivedFrom":[makeQuery(id+"F9.opFillet","BLEND_FACE",FACE,{"disambiguationData":[OSD([subQ0]),TDD([makeQuery(id+"F8.opExtrude","CAP_EDGE",EDGE,{"disambiguationData":[OSD([subQ0])],"isStart":false})])]}),makeQuery(id+"F16.opExtrude","SWEPT_FACE",FACE,{"disambiguationData":[OSD([sQuery(id+"F15.wireOp",EDGE,"E47.1.0")])]})]});}
            var Q21;
            {var subQ0=sQuery(id+"F0.wireOp",EDGE,"E17");Q21=makeQuery(id+"F16.boolean.opBoolean","INTERSECT",EDGE,{"derivedFrom":[makeQuery(id+"F9.opFillet","BLEND_FACE",FACE,{"disambiguationData":[OSD([subQ0]),TDD([makeQuery(id+"F8.opExtrude","CAP_EDGE",EDGE,{"disambiguationData":[OSD([subQ0])],"isStart":false})])]}),makeQuery(id+"F16.opExtrude","SWEPT_FACE",FACE,{"disambiguationData":[OSD([sQuery(id+"F15.wireOp",EDGE,"E46")])]})]});}
            var Q22;
            {var subQ0=sQuery(id+"F0.wireOp",EDGE,"E17");Q22=makeQuery(id+"F16.boolean.opBoolean","INTERSECT",EDGE,{"derivedFrom":[makeQuery(id+"F9.opFillet","BLEND_FACE",FACE,{"disambiguationData":[OSD([subQ0]),TDD([makeQuery(id+"F8.opExtrude","CAP_EDGE",EDGE,{"disambiguationData":[OSD([subQ0])],"isStart":false})])]}),makeQuery(id+"F16.opExtrude","SWEPT_FACE",FACE,{"disambiguationData":[OSD([sQuery(id+"F15.wireOp",EDGE,"E49.1.39.0")])]})]});}
            var Q23;
            {var subQ0=sQuery(id+"F0.wireOp",EDGE,"E17");Q23=makeQuery(id+"F16.boolean.opBoolean","INTERSECT",EDGE,{"derivedFrom":[makeQuery(id+"F9.opFillet","BLEND_FACE",FACE,{"disambiguationData":[OSD([subQ0]),TDD([makeQuery(id+"F8.opExtrude","CAP_EDGE",EDGE,{"disambiguationData":[OSD([subQ0])],"isStart":false})])]}),makeQuery(id+"F16.opExtrude","SWEPT_FACE",FACE,{"disambiguationData":[OSD([sQuery(id+"F15.wireOp",EDGE,"E49.1.38.0")])]})]});}
            var Q24;
            {var subQ0=sQuery(id+"F0.wireOp",EDGE,"E17");Q24=makeQuery(id+"F16.boolean.opBoolean","INTERSECT",EDGE,{"derivedFrom":[makeQuery(id+"F9.opFillet","BLEND_FACE",FACE,{"disambiguationData":[OSD([subQ0]),TDD([makeQuery(id+"F8.opExtrude","CAP_EDGE",EDGE,{"disambiguationData":[OSD([subQ0])],"isStart":false})])]}),makeQuery(id+"F16.opExtrude","SWEPT_FACE",FACE,{"disambiguationData":[OSD([sQuery(id+"F15.wireOp",EDGE,"E49.1.37.0")])]})]});}
            var Q25;
            {var subQ0=sQuery(id+"F0.wireOp",EDGE,"E17");Q25=makeQuery(id+"F16.boolean.opBoolean","INTERSECT",EDGE,{"derivedFrom":[makeQuery(id+"F9.opFillet","BLEND_FACE",FACE,{"disambiguationData":[OSD([subQ0]),TDD([makeQuery(id+"F8.opExtrude","CAP_EDGE",EDGE,{"disambiguationData":[OSD([subQ0])],"isStart":false})])]}),makeQuery(id+"F16.opExtrude","SWEPT_FACE",FACE,{"disambiguationData":[OSD([sQuery(id+"F15.wireOp",EDGE,"E49.1.36.0")])]})]});}
            var Q26;
            {var subQ0=sQuery(id+"F0.wireOp",EDGE,"E17");Q26=makeQuery(id+"F16.boolean.opBoolean","INTERSECT",EDGE,{"derivedFrom":[makeQuery(id+"F9.opFillet","BLEND_FACE",FACE,{"disambiguationData":[OSD([subQ0]),TDD([makeQuery(id+"F8.opExtrude","CAP_EDGE",EDGE,{"disambiguationData":[OSD([subQ0])],"isStart":false})])]}),makeQuery(id+"F16.opExtrude","SWEPT_FACE",FACE,{"disambiguationData":[OSD([sQuery(id+"F15.wireOp",EDGE,"E49.1.34.0")])]})]});}
            var Q27;
            {var subQ0=sQuery(id+"F0.wireOp",EDGE,"E17");Q27=makeQuery(id+"F16.boolean.opBoolean","INTERSECT",EDGE,{"derivedFrom":[makeQuery(id+"F9.opFillet","BLEND_FACE",FACE,{"disambiguationData":[OSD([subQ0]),TDD([makeQuery(id+"F8.opExtrude","CAP_EDGE",EDGE,{"disambiguationData":[OSD([subQ0])],"isStart":false})])]}),makeQuery(id+"F16.opExtrude","SWEPT_FACE",FACE,{"disambiguationData":[OSD([sQuery(id+"F15.wireOp",EDGE,"E49.1.33.0")])]})]});}
            var Q28;
            {var subQ0=sQuery(id+"F0.wireOp",EDGE,"E17");Q28=makeQuery(id+"F16.boolean.opBoolean","INTERSECT",EDGE,{"derivedFrom":[makeQuery(id+"F9.opFillet","BLEND_FACE",FACE,{"disambiguationData":[OSD([subQ0]),TDD([makeQuery(id+"F8.opExtrude","CAP_EDGE",EDGE,{"disambiguationData":[OSD([subQ0])],"isStart":false})])]}),makeQuery(id+"F16.opExtrude","SWEPT_FACE",FACE,{"disambiguationData":[OSD([sQuery(id+"F15.wireOp",EDGE,"E49.1.32.0")])]})]});}
            var Q29;
            {var subQ0=sQuery(id+"F0.wireOp",EDGE,"E17");Q29=makeQuery(id+"F16.boolean.opBoolean","INTERSECT",EDGE,{"derivedFrom":[makeQuery(id+"F9.opFillet","BLEND_FACE",FACE,{"disambiguationData":[OSD([subQ0]),TDD([makeQuery(id+"F8.opExtrude","CAP_EDGE",EDGE,{"disambiguationData":[OSD([subQ0])],"isStart":false})])]}),makeQuery(id+"F16.opExtrude","SWEPT_FACE",FACE,{"disambiguationData":[OSD([sQuery(id+"F15.wireOp",EDGE,"E49.1.31.0")])]})]});}
            var Q30;
            {var subQ0=sQuery(id+"F0.wireOp",EDGE,"E17");Q30=makeQuery(id+"F16.boolean.opBoolean","INTERSECT",EDGE,{"derivedFrom":[makeQuery(id+"F9.opFillet","BLEND_FACE",FACE,{"disambiguationData":[OSD([subQ0]),TDD([makeQuery(id+"F8.opExtrude","CAP_EDGE",EDGE,{"disambiguationData":[OSD([subQ0])],"isStart":false})])]}),makeQuery(id+"F16.opExtrude","SWEPT_FACE",FACE,{"disambiguationData":[OSD([sQuery(id+"F15.wireOp",EDGE,"E49.1.30.0")])]})]});}
            var Q31;
            {var subQ0=sQuery(id+"F0.wireOp",EDGE,"E17");Q31=makeQuery(id+"F16.boolean.opBoolean","INTERSECT",EDGE,{"derivedFrom":[makeQuery(id+"F9.opFillet","BLEND_FACE",FACE,{"disambiguationData":[OSD([subQ0]),TDD([makeQuery(id+"F8.opExtrude","CAP_EDGE",EDGE,{"disambiguationData":[OSD([subQ0])],"isStart":false})])]}),makeQuery(id+"F16.opExtrude","SWEPT_FACE",FACE,{"disambiguationData":[OSD([sQuery(id+"F15.wireOp",EDGE,"E48.1.29.0")])]})]});}
            var Q32;
            {var subQ0=sQuery(id+"F0.wireOp",EDGE,"E17");Q32=makeQuery(id+"F16.boolean.opBoolean","INTERSECT",EDGE,{"derivedFrom":[makeQuery(id+"F9.opFillet","BLEND_FACE",FACE,{"disambiguationData":[OSD([subQ0]),TDD([makeQuery(id+"F8.opExtrude","CAP_EDGE",EDGE,{"disambiguationData":[OSD([subQ0])],"isStart":false})])]}),makeQuery(id+"F16.opExtrude","SWEPT_FACE",FACE,{"disambiguationData":[OSD([sQuery(id+"F15.wireOp",EDGE,"E48.1.28.0")])]})]});}
            var Q33;
            {var subQ0=sQuery(id+"F0.wireOp",EDGE,"E17");Q33=makeQuery(id+"F16.boolean.opBoolean","INTERSECT",EDGE,{"derivedFrom":[makeQuery(id+"F9.opFillet","BLEND_FACE",FACE,{"disambiguationData":[OSD([subQ0]),TDD([makeQuery(id+"F8.opExtrude","CAP_EDGE",EDGE,{"disambiguationData":[OSD([subQ0])],"isStart":false})])]}),makeQuery(id+"F16.opExtrude","SWEPT_FACE",FACE,{"disambiguationData":[OSD([sQuery(id+"F15.wireOp",EDGE,"E48.1.27.0")])]})]});}
            var Q34;
            {var subQ0=sQuery(id+"F0.wireOp",EDGE,"E17");Q34=makeQuery(id+"F16.boolean.opBoolean","INTERSECT",EDGE,{"derivedFrom":[makeQuery(id+"F9.opFillet","BLEND_FACE",FACE,{"disambiguationData":[OSD([subQ0]),TDD([makeQuery(id+"F8.opExtrude","CAP_EDGE",EDGE,{"disambiguationData":[OSD([subQ0])],"isStart":false})])]}),makeQuery(id+"F16.opExtrude","SWEPT_FACE",FACE,{"disambiguationData":[OSD([sQuery(id+"F15.wireOp",EDGE,"E48.1.26.0")])]})]});}
            var Q35;
            {var subQ0=sQuery(id+"F0.wireOp",EDGE,"E17");Q35=makeQuery(id+"F16.boolean.opBoolean","INTERSECT",EDGE,{"derivedFrom":[makeQuery(id+"F9.opFillet","BLEND_FACE",FACE,{"disambiguationData":[OSD([subQ0]),TDD([makeQuery(id+"F8.opExtrude","CAP_EDGE",EDGE,{"disambiguationData":[OSD([subQ0])],"isStart":false})])]}),makeQuery(id+"F16.opExtrude","SWEPT_FACE",FACE,{"disambiguationData":[OSD([sQuery(id+"F15.wireOp",EDGE,"E48.1.25.0")])]})]});}
            var Q36;
            {var subQ0=sQuery(id+"F0.wireOp",EDGE,"E17");Q36=makeQuery(id+"F16.boolean.opBoolean","INTERSECT",EDGE,{"derivedFrom":[makeQuery(id+"F9.opFillet","BLEND_FACE",FACE,{"disambiguationData":[OSD([subQ0]),TDD([makeQuery(id+"F8.opExtrude","CAP_EDGE",EDGE,{"disambiguationData":[OSD([subQ0])],"isStart":false})])]}),makeQuery(id+"F16.opExtrude","SWEPT_FACE",FACE,{"disambiguationData":[OSD([sQuery(id+"F15.wireOp",EDGE,"E48.1.24.0")])]})]});}
            var Q37;
            {var subQ0=sQuery(id+"F0.wireOp",EDGE,"E17");Q37=makeQuery(id+"F16.boolean.opBoolean","INTERSECT",EDGE,{"derivedFrom":[makeQuery(id+"F9.opFillet","BLEND_FACE",FACE,{"disambiguationData":[OSD([subQ0]),TDD([makeQuery(id+"F8.opExtrude","CAP_EDGE",EDGE,{"disambiguationData":[OSD([subQ0])],"isStart":false})])]}),makeQuery(id+"F16.opExtrude","SWEPT_FACE",FACE,{"disambiguationData":[OSD([sQuery(id+"F15.wireOp",EDGE,"E48.1.23.0")])]})]});}
            var Q38;
            {var subQ0=sQuery(id+"F0.wireOp",EDGE,"E17");Q38=makeQuery(id+"F16.boolean.opBoolean","INTERSECT",EDGE,{"derivedFrom":[makeQuery(id+"F9.opFillet","BLEND_FACE",FACE,{"disambiguationData":[OSD([subQ0]),TDD([makeQuery(id+"F8.opExtrude","CAP_EDGE",EDGE,{"disambiguationData":[OSD([subQ0])],"isStart":false})])]}),makeQuery(id+"F16.opExtrude","SWEPT_FACE",FACE,{"disambiguationData":[OSD([sQuery(id+"F15.wireOp",EDGE,"E48.1.22.0")])]})]});}
            var Q39;
            {var subQ0=sQuery(id+"F0.wireOp",EDGE,"E17");Q39=makeQuery(id+"F16.boolean.opBoolean","INTERSECT",EDGE,{"derivedFrom":[makeQuery(id+"F9.opFillet","BLEND_FACE",FACE,{"disambiguationData":[OSD([subQ0]),TDD([makeQuery(id+"F8.opExtrude","CAP_EDGE",EDGE,{"disambiguationData":[OSD([subQ0])],"isStart":false})])]}),makeQuery(id+"F16.opExtrude","SWEPT_FACE",FACE,{"disambiguationData":[OSD([sQuery(id+"F15.wireOp",EDGE,"E49.1.35.0")])]})]});}
            fillet(context, id + "F18", {"entities" : qUnion([Q0, Q1, Q2, Q3, Q4, Q5, Q6, Q7, Q8, Q9, Q10, Q11, Q12, Q13, Q14, Q15, Q16, Q17, Q18, Q19, Q20, Q21, Q22, Q23, Q24, Q25, Q26, Q27, Q28, Q29, Q30, Q31, Q32, Q33, Q34, Q35, Q36, Q37, Q38, Q39]), "tangentPropagation" : true, "radius" : .8 * mm, "defaultsChanged" : true, "vertexSettings" : [], "allowEdgeOverflow" : false});
        }
    });
